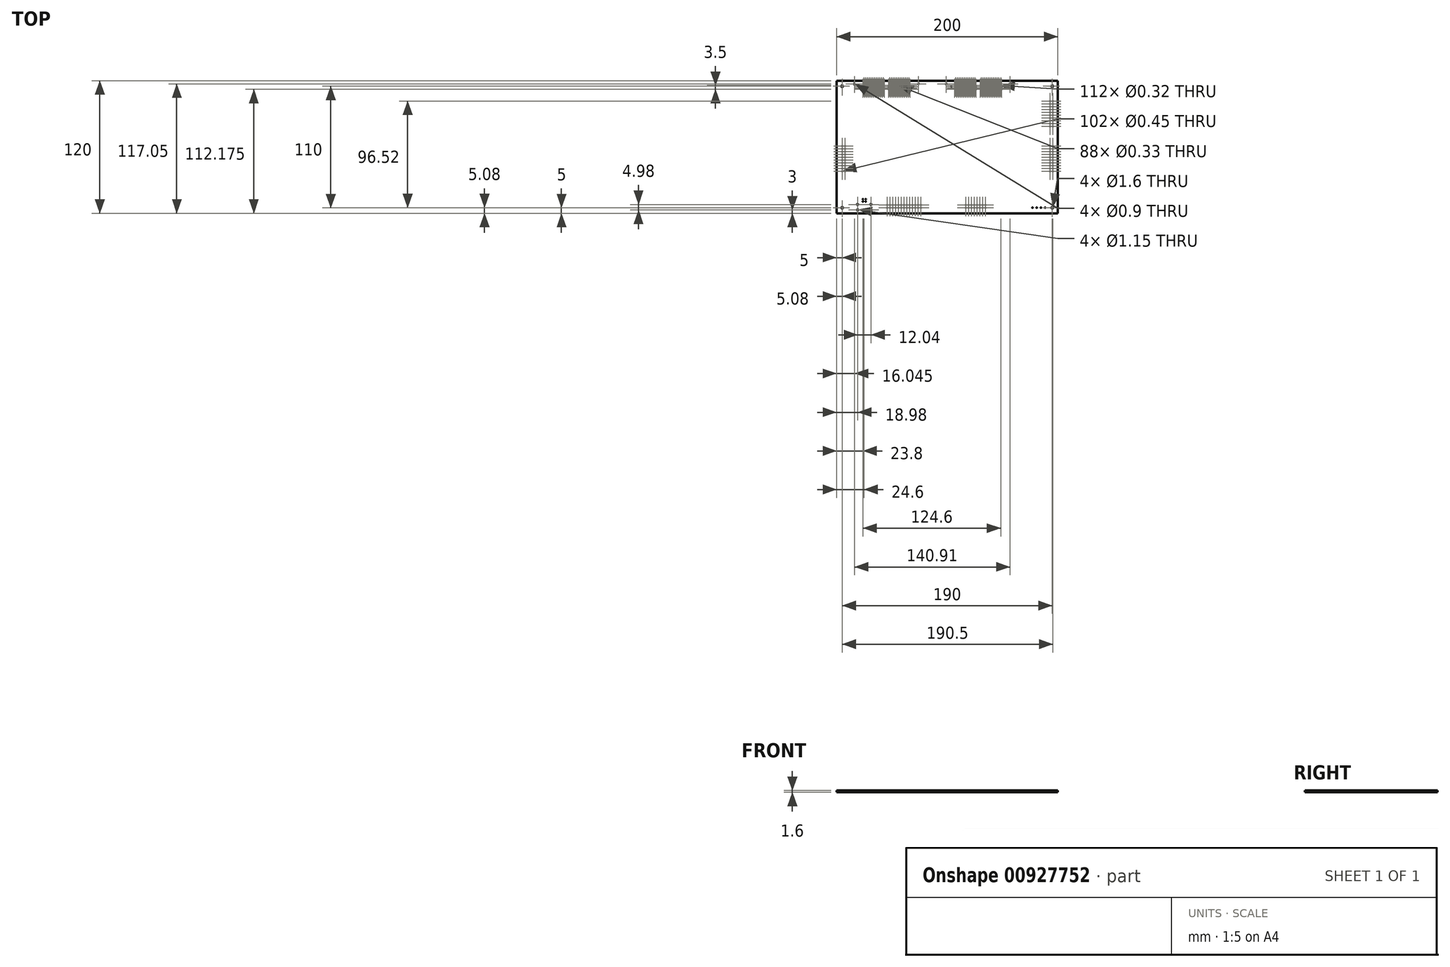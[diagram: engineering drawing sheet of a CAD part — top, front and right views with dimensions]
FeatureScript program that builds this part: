
annotation { "Feature Type Name" : "Feature", "Feature Type Description" : "" }
export const myFeature = defineFeature(function(context is Context, id is Id, definition is map)
    precondition{}
    {
        {
            var Q0;
            Q0=qCreatedBy(makeId("Top.planeOp"),FACE);
            var sketch = newSketch(context, id + "F0", { "sketchPlane" : qUnion([Q0])});
            skLineSegment(sketch, "E0", {"start": v(-100, -60) * mm, "end": v(100, -60) * mm});
            skLineSegment(sketch, "E1", {"start": v(100, -60) * mm, "end": v(100, 60) * mm});
            skLineSegment(sketch, "E2", {"start": v(100, 60) * mm, "end": v(-100, 60) * mm});
            skLineSegment(sketch, "E3", {"start": v(-100, 60) * mm, "end": v(-100, -60) * mm});
            skArc(sketch, "E4", {"start": v(-95.8, 55) * mm, "mid": v(-95, 54.2) * mm, "end": v(-94.2, 55) * mm});
            skArc(sketch, "E5", {"start": v(-94.2, 55) * mm, "mid": v(-95, 55.8) * mm, "end": v(-95.8, 55) * mm});
            skArc(sketch, "E6", {"start": v(-95.8, -55) * mm, "mid": v(-95, -55.8) * mm, "end": v(-94.2, -55) * mm});
            skArc(sketch, "E7", {"start": v(-94.2, -55) * mm, "mid": v(-95, -54.2) * mm, "end": v(-95.8, -55) * mm});
            skArc(sketch, "E8", {"start": v(94.2, -55) * mm, "mid": v(95, -55.8) * mm, "end": v(95.8, -55) * mm});
            skArc(sketch, "E9", {"start": v(95.8, -55) * mm, "mid": v(95, -54.2) * mm, "end": v(94.2, -55) * mm});
            skArc(sketch, "E10", {"start": v(94.2, 55) * mm, "mid": v(95, 54.2) * mm, "end": v(95.8, 55) * mm});
            skArc(sketch, "E11", {"start": v(95.8, 55) * mm, "mid": v(95, 55.8) * mm, "end": v(94.2, 55) * mm});
            skArc(sketch, "E12", {"start": v(-76.36, 54.53) * mm, "mid": v(-76.2, 54.36) * mm, "end": v(-76.04, 54.53) * mm});
            skArc(sketch, "E13", {"start": v(-76.04, 54.53) * mm, "mid": v(-76.2, 54.69) * mm, "end": v(-76.36, 54.53) * mm});
            skArc(sketch, "E14", {"start": v(-76.36, 52.18) * mm, "mid": v(-76.2, 52.01) * mm, "end": v(-76.04, 52.18) * mm});
            skArc(sketch, "E15", {"start": v(-76.04, 52.18) * mm, "mid": v(-76.2, 52.34) * mm, "end": v(-76.36, 52.18) * mm});
            skArc(sketch, "E16", {"start": v(-75.56, 53.33) * mm, "mid": v(-75.4, 53.16) * mm, "end": v(-75.24, 53.33) * mm});
            skArc(sketch, "E17", {"start": v(-75.24, 53.33) * mm, "mid": v(-75.4, 53.49) * mm, "end": v(-75.56, 53.33) * mm});
            skArc(sketch, "E18", {"start": v(-75.56, 55.68) * mm, "mid": v(-75.4, 55.51) * mm, "end": v(-75.24, 55.68) * mm});
            skArc(sketch, "E19", {"start": v(-75.24, 55.68) * mm, "mid": v(-75.4, 55.84) * mm, "end": v(-75.56, 55.68) * mm});
            skArc(sketch, "E20", {"start": v(-74.76, 54.53) * mm, "mid": v(-74.6, 54.36) * mm, "end": v(-74.44, 54.53) * mm});
            skArc(sketch, "E21", {"start": v(-74.44, 54.53) * mm, "mid": v(-74.6, 54.69) * mm, "end": v(-74.76, 54.53) * mm});
            skArc(sketch, "E22", {"start": v(-74.76, 52.18) * mm, "mid": v(-74.6, 52.01) * mm, "end": v(-74.44, 52.18) * mm});
            skArc(sketch, "E23", {"start": v(-74.44, 52.18) * mm, "mid": v(-74.6, 52.34) * mm, "end": v(-74.76, 52.18) * mm});
            skArc(sketch, "E24", {"start": v(-73.96, 53.33) * mm, "mid": v(-73.8, 53.16) * mm, "end": v(-73.64, 53.33) * mm});
            skArc(sketch, "E25", {"start": v(-73.64, 53.33) * mm, "mid": v(-73.8, 53.49) * mm, "end": v(-73.96, 53.33) * mm});
            skArc(sketch, "E26", {"start": v(-73.96, 55.68) * mm, "mid": v(-73.8, 55.51) * mm, "end": v(-73.64, 55.68) * mm});
            skArc(sketch, "E27", {"start": v(-73.64, 55.68) * mm, "mid": v(-73.8, 55.84) * mm, "end": v(-73.96, 55.68) * mm});
            skArc(sketch, "E28", {"start": v(-73.16, 54.53) * mm, "mid": v(-73, 54.36) * mm, "end": v(-72.84, 54.53) * mm});
            skArc(sketch, "E29", {"start": v(-72.84, 54.53) * mm, "mid": v(-73, 54.69) * mm, "end": v(-73.16, 54.53) * mm});
            skArc(sketch, "E30", {"start": v(-73.16, 52.18) * mm, "mid": v(-73, 52.01) * mm, "end": v(-72.84, 52.18) * mm});
            skArc(sketch, "E31", {"start": v(-72.84, 52.18) * mm, "mid": v(-73, 52.34) * mm, "end": v(-73.16, 52.18) * mm});
            skArc(sketch, "E32", {"start": v(-72.36, 53.33) * mm, "mid": v(-72.2, 53.16) * mm, "end": v(-72.04, 53.33) * mm});
            skArc(sketch, "E33", {"start": v(-72.04, 53.33) * mm, "mid": v(-72.2, 53.49) * mm, "end": v(-72.36, 53.33) * mm});
            skArc(sketch, "E34", {"start": v(-72.36, 55.68) * mm, "mid": v(-72.2, 55.51) * mm, "end": v(-72.04, 55.68) * mm});
            skArc(sketch, "E35", {"start": v(-72.04, 55.68) * mm, "mid": v(-72.2, 55.84) * mm, "end": v(-72.36, 55.68) * mm});
            skArc(sketch, "E36", {"start": v(-71.56, 54.53) * mm, "mid": v(-71.4, 54.36) * mm, "end": v(-71.24, 54.53) * mm});
            skArc(sketch, "E37", {"start": v(-71.24, 54.53) * mm, "mid": v(-71.4, 54.69) * mm, "end": v(-71.56, 54.53) * mm});
            skArc(sketch, "E38", {"start": v(-71.56, 52.18) * mm, "mid": v(-71.4, 52.01) * mm, "end": v(-71.24, 52.18) * mm});
            skArc(sketch, "E39", {"start": v(-71.24, 52.18) * mm, "mid": v(-71.4, 52.34) * mm, "end": v(-71.56, 52.18) * mm});
            skArc(sketch, "E40", {"start": v(-70.76, 53.33) * mm, "mid": v(-70.6, 53.16) * mm, "end": v(-70.44, 53.33) * mm});
            skArc(sketch, "E41", {"start": v(-70.44, 53.33) * mm, "mid": v(-70.6, 53.49) * mm, "end": v(-70.76, 53.33) * mm});
            skArc(sketch, "E42", {"start": v(-70.76, 55.68) * mm, "mid": v(-70.6, 55.51) * mm, "end": v(-70.44, 55.68) * mm});
            skArc(sketch, "E43", {"start": v(-70.44, 55.68) * mm, "mid": v(-70.6, 55.84) * mm, "end": v(-70.76, 55.68) * mm});
            skArc(sketch, "E44", {"start": v(-69.96, 54.53) * mm, "mid": v(-69.8, 54.36) * mm, "end": v(-69.64, 54.53) * mm});
            skArc(sketch, "E45", {"start": v(-69.64, 54.53) * mm, "mid": v(-69.8, 54.69) * mm, "end": v(-69.96, 54.53) * mm});
            skArc(sketch, "E46", {"start": v(-69.96, 52.18) * mm, "mid": v(-69.8, 52.01) * mm, "end": v(-69.64, 52.18) * mm});
            skArc(sketch, "E47", {"start": v(-69.64, 52.18) * mm, "mid": v(-69.8, 52.34) * mm, "end": v(-69.96, 52.18) * mm});
            skArc(sketch, "E48", {"start": v(-69.16, 53.33) * mm, "mid": v(-69, 53.16) * mm, "end": v(-68.84, 53.33) * mm});
            skArc(sketch, "E49", {"start": v(-68.84, 53.33) * mm, "mid": v(-69, 53.49) * mm, "end": v(-69.16, 53.33) * mm});
            skArc(sketch, "E50", {"start": v(-69.16, 55.68) * mm, "mid": v(-69, 55.51) * mm, "end": v(-68.84, 55.68) * mm});
            skArc(sketch, "E51", {"start": v(-68.84, 55.68) * mm, "mid": v(-69, 55.84) * mm, "end": v(-69.16, 55.68) * mm});
            skArc(sketch, "E52", {"start": v(-68.36, 54.53) * mm, "mid": v(-68.2, 54.36) * mm, "end": v(-68.04, 54.53) * mm});
            skArc(sketch, "E53", {"start": v(-68.04, 54.53) * mm, "mid": v(-68.2, 54.69) * mm, "end": v(-68.36, 54.53) * mm});
            skArc(sketch, "E54", {"start": v(-68.36, 52.18) * mm, "mid": v(-68.2, 52.01) * mm, "end": v(-68.04, 52.18) * mm});
            skArc(sketch, "E55", {"start": v(-68.04, 52.18) * mm, "mid": v(-68.2, 52.34) * mm, "end": v(-68.36, 52.18) * mm});
            skArc(sketch, "E56", {"start": v(-67.56, 53.33) * mm, "mid": v(-67.4, 53.16) * mm, "end": v(-67.24, 53.33) * mm});
            skArc(sketch, "E57", {"start": v(-67.24, 53.33) * mm, "mid": v(-67.4, 53.49) * mm, "end": v(-67.56, 53.33) * mm});
            skArc(sketch, "E58", {"start": v(-67.56, 55.68) * mm, "mid": v(-67.4, 55.51) * mm, "end": v(-67.24, 55.68) * mm});
            skArc(sketch, "E59", {"start": v(-67.24, 55.68) * mm, "mid": v(-67.4, 55.84) * mm, "end": v(-67.56, 55.68) * mm});
            skArc(sketch, "E60", {"start": v(-66.76, 54.53) * mm, "mid": v(-66.6, 54.36) * mm, "end": v(-66.44, 54.53) * mm});
            skArc(sketch, "E61", {"start": v(-66.44, 54.53) * mm, "mid": v(-66.6, 54.69) * mm, "end": v(-66.76, 54.53) * mm});
            skArc(sketch, "E62", {"start": v(-66.76, 52.18) * mm, "mid": v(-66.6, 52.01) * mm, "end": v(-66.44, 52.18) * mm});
            skArc(sketch, "E63", {"start": v(-66.44, 52.18) * mm, "mid": v(-66.6, 52.34) * mm, "end": v(-66.76, 52.18) * mm});
            skArc(sketch, "E64", {"start": v(-65.96, 53.33) * mm, "mid": v(-65.8, 53.16) * mm, "end": v(-65.64, 53.33) * mm});
            skArc(sketch, "E65", {"start": v(-65.64, 53.33) * mm, "mid": v(-65.8, 53.49) * mm, "end": v(-65.96, 53.33) * mm});
            skArc(sketch, "E66", {"start": v(-65.96, 55.68) * mm, "mid": v(-65.8, 55.51) * mm, "end": v(-65.64, 55.68) * mm});
            skArc(sketch, "E67", {"start": v(-65.64, 55.68) * mm, "mid": v(-65.8, 55.84) * mm, "end": v(-65.96, 55.68) * mm});
            skArc(sketch, "E68", {"start": v(-65.16, 54.53) * mm, "mid": v(-65, 54.36) * mm, "end": v(-64.84, 54.53) * mm});
            skArc(sketch, "E69", {"start": v(-64.84, 54.53) * mm, "mid": v(-65, 54.69) * mm, "end": v(-65.16, 54.53) * mm});
            skArc(sketch, "E70", {"start": v(-65.16, 52.18) * mm, "mid": v(-65, 52.01) * mm, "end": v(-64.84, 52.18) * mm});
            skArc(sketch, "E71", {"start": v(-64.84, 52.18) * mm, "mid": v(-65, 52.34) * mm, "end": v(-65.16, 52.18) * mm});
            skArc(sketch, "E72", {"start": v(-64.36, 53.33) * mm, "mid": v(-64.2, 53.16) * mm, "end": v(-64.04, 53.33) * mm});
            skArc(sketch, "E73", {"start": v(-64.04, 53.33) * mm, "mid": v(-64.2, 53.49) * mm, "end": v(-64.36, 53.33) * mm});
            skArc(sketch, "E74", {"start": v(-64.36, 55.68) * mm, "mid": v(-64.2, 55.51) * mm, "end": v(-64.04, 55.68) * mm});
            skArc(sketch, "E75", {"start": v(-64.04, 55.68) * mm, "mid": v(-64.2, 55.84) * mm, "end": v(-64.36, 55.68) * mm});
            skArc(sketch, "E76", {"start": v(-63.56, 54.53) * mm, "mid": v(-63.4, 54.36) * mm, "end": v(-63.24, 54.53) * mm});
            skArc(sketch, "E77", {"start": v(-63.24, 54.53) * mm, "mid": v(-63.4, 54.69) * mm, "end": v(-63.56, 54.53) * mm});
            skArc(sketch, "E78", {"start": v(-63.56, 52.18) * mm, "mid": v(-63.4, 52.01) * mm, "end": v(-63.24, 52.18) * mm});
            skArc(sketch, "E79", {"start": v(-63.24, 52.18) * mm, "mid": v(-63.4, 52.34) * mm, "end": v(-63.56, 52.18) * mm});
            skArc(sketch, "E80", {"start": v(-62.76, 53.33) * mm, "mid": v(-62.6, 53.16) * mm, "end": v(-62.44, 53.33) * mm});
            skArc(sketch, "E81", {"start": v(-62.44, 53.33) * mm, "mid": v(-62.6, 53.49) * mm, "end": v(-62.76, 53.33) * mm});
            skArc(sketch, "E82", {"start": v(-62.76, 55.68) * mm, "mid": v(-62.6, 55.51) * mm, "end": v(-62.44, 55.68) * mm});
            skArc(sketch, "E83", {"start": v(-62.44, 55.68) * mm, "mid": v(-62.6, 55.84) * mm, "end": v(-62.76, 55.68) * mm});
            skArc(sketch, "E84", {"start": v(-61.96, 54.53) * mm, "mid": v(-61.8, 54.36) * mm, "end": v(-61.64, 54.53) * mm});
            skArc(sketch, "E85", {"start": v(-61.64, 54.53) * mm, "mid": v(-61.8, 54.69) * mm, "end": v(-61.96, 54.53) * mm});
            skArc(sketch, "E86", {"start": v(-61.96, 52.18) * mm, "mid": v(-61.8, 52.01) * mm, "end": v(-61.64, 52.18) * mm});
            skArc(sketch, "E87", {"start": v(-61.64, 52.18) * mm, "mid": v(-61.8, 52.34) * mm, "end": v(-61.96, 52.18) * mm});
            skArc(sketch, "E88", {"start": v(-61.16, 53.33) * mm, "mid": v(-61, 53.16) * mm, "end": v(-60.84, 53.33) * mm});
            skArc(sketch, "E89", {"start": v(-60.84, 53.33) * mm, "mid": v(-61, 53.49) * mm, "end": v(-61.16, 53.33) * mm});
            skArc(sketch, "E90", {"start": v(-61.16, 55.68) * mm, "mid": v(-61, 55.51) * mm, "end": v(-60.84, 55.68) * mm});
            skArc(sketch, "E91", {"start": v(-60.84, 55.68) * mm, "mid": v(-61, 55.84) * mm, "end": v(-61.16, 55.68) * mm});
            skArc(sketch, "E92", {"start": v(-60.36, 54.53) * mm, "mid": v(-60.2, 54.36) * mm, "end": v(-60.04, 54.53) * mm});
            skArc(sketch, "E93", {"start": v(-60.04, 54.53) * mm, "mid": v(-60.2, 54.69) * mm, "end": v(-60.36, 54.53) * mm});
            skArc(sketch, "E94", {"start": v(-60.36, 52.18) * mm, "mid": v(-60.2, 52.01) * mm, "end": v(-60.04, 52.18) * mm});
            skArc(sketch, "E95", {"start": v(-60.04, 52.18) * mm, "mid": v(-60.2, 52.34) * mm, "end": v(-60.36, 52.18) * mm});
            skArc(sketch, "E96", {"start": v(-59.56, 53.33) * mm, "mid": v(-59.4, 53.16) * mm, "end": v(-59.24, 53.33) * mm});
            skArc(sketch, "E97", {"start": v(-59.24, 53.33) * mm, "mid": v(-59.4, 53.49) * mm, "end": v(-59.56, 53.33) * mm});
            skArc(sketch, "E98", {"start": v(-59.56, 55.68) * mm, "mid": v(-59.4, 55.51) * mm, "end": v(-59.24, 55.68) * mm});
            skArc(sketch, "E99", {"start": v(-59.24, 55.68) * mm, "mid": v(-59.4, 55.84) * mm, "end": v(-59.56, 55.68) * mm});
            skArc(sketch, "E100", {"start": v(-58.76, 54.53) * mm, "mid": v(-58.6, 54.36) * mm, "end": v(-58.44, 54.53) * mm});
            skArc(sketch, "E101", {"start": v(-58.44, 54.53) * mm, "mid": v(-58.6, 54.69) * mm, "end": v(-58.76, 54.53) * mm});
            skArc(sketch, "E102", {"start": v(-58.76, 52.18) * mm, "mid": v(-58.6, 52.01) * mm, "end": v(-58.44, 52.18) * mm});
            skArc(sketch, "E103", {"start": v(-58.44, 52.18) * mm, "mid": v(-58.6, 52.34) * mm, "end": v(-58.76, 52.18) * mm});
            skArc(sketch, "E104", {"start": v(-57.96, 53.33) * mm, "mid": v(-57.8, 53.16) * mm, "end": v(-57.64, 53.33) * mm});
            skArc(sketch, "E105", {"start": v(-57.64, 53.33) * mm, "mid": v(-57.8, 53.49) * mm, "end": v(-57.96, 53.33) * mm});
            skArc(sketch, "E106", {"start": v(-57.96, 55.68) * mm, "mid": v(-57.8, 55.51) * mm, "end": v(-57.64, 55.68) * mm});
            skArc(sketch, "E107", {"start": v(-57.64, 55.68) * mm, "mid": v(-57.8, 55.84) * mm, "end": v(-57.96, 55.68) * mm});
            skArc(sketch, "E108", {"start": v(-57.16, 54.53) * mm, "mid": v(-57, 54.36) * mm, "end": v(-56.84, 54.53) * mm});
            skArc(sketch, "E109", {"start": v(-56.84, 54.53) * mm, "mid": v(-57, 54.69) * mm, "end": v(-57.16, 54.53) * mm});
            skArc(sketch, "E110", {"start": v(-57.16, 52.18) * mm, "mid": v(-57, 52.01) * mm, "end": v(-56.84, 52.18) * mm});
            skArc(sketch, "E111", {"start": v(-56.84, 52.18) * mm, "mid": v(-57, 52.34) * mm, "end": v(-57.16, 52.18) * mm});
            skArc(sketch, "E112", {"start": v(-53.16, 52.18) * mm, "mid": v(-53, 52.01) * mm, "end": v(-52.84, 52.18) * mm});
            skArc(sketch, "E113", {"start": v(-52.84, 52.18) * mm, "mid": v(-53, 52.34) * mm, "end": v(-53.16, 52.18) * mm});
            skArc(sketch, "E114", {"start": v(-53.16, 54.53) * mm, "mid": v(-53, 54.36) * mm, "end": v(-52.84, 54.53) * mm});
            skArc(sketch, "E115", {"start": v(-52.84, 54.53) * mm, "mid": v(-53, 54.69) * mm, "end": v(-53.16, 54.53) * mm});
            skArc(sketch, "E116", {"start": v(-52.36, 55.68) * mm, "mid": v(-52.2, 55.51) * mm, "end": v(-52.04, 55.68) * mm});
            skArc(sketch, "E117", {"start": v(-52.04, 55.68) * mm, "mid": v(-52.2, 55.84) * mm, "end": v(-52.36, 55.68) * mm});
            skArc(sketch, "E118", {"start": v(-52.36, 53.33) * mm, "mid": v(-52.2, 53.16) * mm, "end": v(-52.04, 53.33) * mm});
            skArc(sketch, "E119", {"start": v(-52.04, 53.33) * mm, "mid": v(-52.2, 53.49) * mm, "end": v(-52.36, 53.33) * mm});
            skArc(sketch, "E120", {"start": v(-51.56, 52.18) * mm, "mid": v(-51.4, 52.01) * mm, "end": v(-51.24, 52.18) * mm});
            skArc(sketch, "E121", {"start": v(-51.24, 52.18) * mm, "mid": v(-51.4, 52.34) * mm, "end": v(-51.56, 52.18) * mm});
            skArc(sketch, "E122", {"start": v(-51.56, 54.53) * mm, "mid": v(-51.4, 54.36) * mm, "end": v(-51.24, 54.53) * mm});
            skArc(sketch, "E123", {"start": v(-51.24, 54.53) * mm, "mid": v(-51.4, 54.69) * mm, "end": v(-51.56, 54.53) * mm});
            skArc(sketch, "E124", {"start": v(-50.76, 55.68) * mm, "mid": v(-50.6, 55.51) * mm, "end": v(-50.44, 55.68) * mm});
            skArc(sketch, "E125", {"start": v(-50.44, 55.68) * mm, "mid": v(-50.6, 55.84) * mm, "end": v(-50.76, 55.68) * mm});
            skArc(sketch, "E126", {"start": v(-50.76, 53.33) * mm, "mid": v(-50.6, 53.16) * mm, "end": v(-50.44, 53.33) * mm});
            skArc(sketch, "E127", {"start": v(-50.44, 53.33) * mm, "mid": v(-50.6, 53.49) * mm, "end": v(-50.76, 53.33) * mm});
            skArc(sketch, "E128", {"start": v(-49.96, 52.18) * mm, "mid": v(-49.8, 52.01) * mm, "end": v(-49.64, 52.18) * mm});
            skArc(sketch, "E129", {"start": v(-49.64, 52.18) * mm, "mid": v(-49.8, 52.34) * mm, "end": v(-49.96, 52.18) * mm});
            skArc(sketch, "E130", {"start": v(-49.96, 54.53) * mm, "mid": v(-49.8, 54.36) * mm, "end": v(-49.64, 54.53) * mm});
            skArc(sketch, "E131", {"start": v(-49.64, 54.53) * mm, "mid": v(-49.8, 54.69) * mm, "end": v(-49.96, 54.53) * mm});
            skArc(sketch, "E132", {"start": v(-49.16, 55.68) * mm, "mid": v(-49, 55.51) * mm, "end": v(-48.84, 55.68) * mm});
            skArc(sketch, "E133", {"start": v(-48.84, 55.68) * mm, "mid": v(-49, 55.84) * mm, "end": v(-49.16, 55.68) * mm});
            skArc(sketch, "E134", {"start": v(-49.16, 53.33) * mm, "mid": v(-49, 53.16) * mm, "end": v(-48.84, 53.33) * mm});
            skArc(sketch, "E135", {"start": v(-48.84, 53.33) * mm, "mid": v(-49, 53.49) * mm, "end": v(-49.16, 53.33) * mm});
            skArc(sketch, "E136", {"start": v(-48.36, 52.18) * mm, "mid": v(-48.2, 52.01) * mm, "end": v(-48.04, 52.18) * mm});
            skArc(sketch, "E137", {"start": v(-48.04, 52.18) * mm, "mid": v(-48.2, 52.34) * mm, "end": v(-48.36, 52.18) * mm});
            skArc(sketch, "E138", {"start": v(-48.36, 54.53) * mm, "mid": v(-48.2, 54.36) * mm, "end": v(-48.04, 54.53) * mm});
            skArc(sketch, "E139", {"start": v(-48.04, 54.53) * mm, "mid": v(-48.2, 54.69) * mm, "end": v(-48.36, 54.53) * mm});
            skArc(sketch, "E140", {"start": v(-47.56, 55.68) * mm, "mid": v(-47.4, 55.51) * mm, "end": v(-47.24, 55.68) * mm});
            skArc(sketch, "E141", {"start": v(-47.24, 55.68) * mm, "mid": v(-47.4, 55.84) * mm, "end": v(-47.56, 55.68) * mm});
            skArc(sketch, "E142", {"start": v(-47.56, 53.33) * mm, "mid": v(-47.4, 53.16) * mm, "end": v(-47.24, 53.33) * mm});
            skArc(sketch, "E143", {"start": v(-47.24, 53.33) * mm, "mid": v(-47.4, 53.49) * mm, "end": v(-47.56, 53.33) * mm});
            skArc(sketch, "E144", {"start": v(-46.76, 52.18) * mm, "mid": v(-46.6, 52.01) * mm, "end": v(-46.44, 52.18) * mm});
            skArc(sketch, "E145", {"start": v(-46.44, 52.18) * mm, "mid": v(-46.6, 52.34) * mm, "end": v(-46.76, 52.18) * mm});
            skArc(sketch, "E146", {"start": v(-46.76, 54.53) * mm, "mid": v(-46.6, 54.36) * mm, "end": v(-46.44, 54.53) * mm});
            skArc(sketch, "E147", {"start": v(-46.44, 54.53) * mm, "mid": v(-46.6, 54.69) * mm, "end": v(-46.76, 54.53) * mm});
            skArc(sketch, "E148", {"start": v(-45.96, 55.68) * mm, "mid": v(-45.8, 55.51) * mm, "end": v(-45.64, 55.68) * mm});
            skArc(sketch, "E149", {"start": v(-45.64, 55.68) * mm, "mid": v(-45.8, 55.84) * mm, "end": v(-45.96, 55.68) * mm});
            skArc(sketch, "E150", {"start": v(-45.96, 53.33) * mm, "mid": v(-45.8, 53.16) * mm, "end": v(-45.64, 53.33) * mm});
            skArc(sketch, "E151", {"start": v(-45.64, 53.33) * mm, "mid": v(-45.8, 53.49) * mm, "end": v(-45.96, 53.33) * mm});
            skArc(sketch, "E152", {"start": v(-45.16, 52.18) * mm, "mid": v(-45, 52.01) * mm, "end": v(-44.84, 52.18) * mm});
            skArc(sketch, "E153", {"start": v(-44.84, 52.18) * mm, "mid": v(-45, 52.34) * mm, "end": v(-45.16, 52.18) * mm});
            skArc(sketch, "E154", {"start": v(-45.16, 54.53) * mm, "mid": v(-45, 54.36) * mm, "end": v(-44.84, 54.53) * mm});
            skArc(sketch, "E155", {"start": v(-44.84, 54.53) * mm, "mid": v(-45, 54.69) * mm, "end": v(-45.16, 54.53) * mm});
            skArc(sketch, "E156", {"start": v(-44.36, 55.68) * mm, "mid": v(-44.2, 55.51) * mm, "end": v(-44.04, 55.68) * mm});
            skArc(sketch, "E157", {"start": v(-44.04, 55.68) * mm, "mid": v(-44.2, 55.84) * mm, "end": v(-44.36, 55.68) * mm});
            skArc(sketch, "E158", {"start": v(-44.36, 53.33) * mm, "mid": v(-44.2, 53.16) * mm, "end": v(-44.04, 53.33) * mm});
            skArc(sketch, "E159", {"start": v(-44.04, 53.33) * mm, "mid": v(-44.2, 53.49) * mm, "end": v(-44.36, 53.33) * mm});
            skArc(sketch, "E160", {"start": v(-43.56, 52.18) * mm, "mid": v(-43.4, 52.01) * mm, "end": v(-43.24, 52.18) * mm});
            skArc(sketch, "E161", {"start": v(-43.24, 52.18) * mm, "mid": v(-43.4, 52.34) * mm, "end": v(-43.56, 52.18) * mm});
            skArc(sketch, "E162", {"start": v(-43.56, 54.53) * mm, "mid": v(-43.4, 54.36) * mm, "end": v(-43.24, 54.53) * mm});
            skArc(sketch, "E163", {"start": v(-43.24, 54.53) * mm, "mid": v(-43.4, 54.69) * mm, "end": v(-43.56, 54.53) * mm});
            skArc(sketch, "E164", {"start": v(-42.76, 55.68) * mm, "mid": v(-42.6, 55.51) * mm, "end": v(-42.44, 55.68) * mm});
            skArc(sketch, "E165", {"start": v(-42.44, 55.68) * mm, "mid": v(-42.6, 55.84) * mm, "end": v(-42.76, 55.68) * mm});
            skArc(sketch, "E166", {"start": v(-42.76, 53.33) * mm, "mid": v(-42.6, 53.16) * mm, "end": v(-42.44, 53.33) * mm});
            skArc(sketch, "E167", {"start": v(-42.44, 53.33) * mm, "mid": v(-42.6, 53.49) * mm, "end": v(-42.76, 53.33) * mm});
            skArc(sketch, "E168", {"start": v(-41.96, 52.18) * mm, "mid": v(-41.8, 52.01) * mm, "end": v(-41.64, 52.18) * mm});
            skArc(sketch, "E169", {"start": v(-41.64, 52.18) * mm, "mid": v(-41.8, 52.34) * mm, "end": v(-41.96, 52.18) * mm});
            skArc(sketch, "E170", {"start": v(-41.96, 54.53) * mm, "mid": v(-41.8, 54.36) * mm, "end": v(-41.64, 54.53) * mm});
            skArc(sketch, "E171", {"start": v(-41.64, 54.53) * mm, "mid": v(-41.8, 54.69) * mm, "end": v(-41.96, 54.53) * mm});
            skArc(sketch, "E172", {"start": v(-41.16, 55.68) * mm, "mid": v(-41, 55.51) * mm, "end": v(-40.84, 55.68) * mm});
            skArc(sketch, "E173", {"start": v(-40.84, 55.68) * mm, "mid": v(-41, 55.84) * mm, "end": v(-41.16, 55.68) * mm});
            skArc(sketch, "E174", {"start": v(-41.16, 53.33) * mm, "mid": v(-41, 53.16) * mm, "end": v(-40.84, 53.33) * mm});
            skArc(sketch, "E175", {"start": v(-40.84, 53.33) * mm, "mid": v(-41, 53.49) * mm, "end": v(-41.16, 53.33) * mm});
            skArc(sketch, "E176", {"start": v(-40.36, 52.18) * mm, "mid": v(-40.2, 52.01) * mm, "end": v(-40.04, 52.18) * mm});
            skArc(sketch, "E177", {"start": v(-40.04, 52.18) * mm, "mid": v(-40.2, 52.34) * mm, "end": v(-40.36, 52.18) * mm});
            skArc(sketch, "E178", {"start": v(-40.36, 54.53) * mm, "mid": v(-40.2, 54.36) * mm, "end": v(-40.04, 54.53) * mm});
            skArc(sketch, "E179", {"start": v(-40.04, 54.53) * mm, "mid": v(-40.2, 54.69) * mm, "end": v(-40.36, 54.53) * mm});
            skArc(sketch, "E180", {"start": v(-39.56, 55.68) * mm, "mid": v(-39.4, 55.51) * mm, "end": v(-39.24, 55.68) * mm});
            skArc(sketch, "E181", {"start": v(-39.24, 55.68) * mm, "mid": v(-39.4, 55.84) * mm, "end": v(-39.56, 55.68) * mm});
            skArc(sketch, "E182", {"start": v(-39.56, 53.33) * mm, "mid": v(-39.4, 53.16) * mm, "end": v(-39.24, 53.33) * mm});
            skArc(sketch, "E183", {"start": v(-39.24, 53.33) * mm, "mid": v(-39.4, 53.49) * mm, "end": v(-39.56, 53.33) * mm});
            skArc(sketch, "E184", {"start": v(-38.76, 52.18) * mm, "mid": v(-38.6, 52.01) * mm, "end": v(-38.44, 52.18) * mm});
            skArc(sketch, "E185", {"start": v(-38.44, 52.18) * mm, "mid": v(-38.6, 52.34) * mm, "end": v(-38.76, 52.18) * mm});
            skArc(sketch, "E186", {"start": v(-38.76, 54.53) * mm, "mid": v(-38.6, 54.36) * mm, "end": v(-38.44, 54.53) * mm});
            skArc(sketch, "E187", {"start": v(-38.44, 54.53) * mm, "mid": v(-38.6, 54.69) * mm, "end": v(-38.76, 54.53) * mm});
            skArc(sketch, "E188", {"start": v(-37.96, 55.68) * mm, "mid": v(-37.8, 55.51) * mm, "end": v(-37.64, 55.68) * mm});
            skArc(sketch, "E189", {"start": v(-37.64, 55.68) * mm, "mid": v(-37.8, 55.84) * mm, "end": v(-37.96, 55.68) * mm});
            skArc(sketch, "E190", {"start": v(-37.96, 53.33) * mm, "mid": v(-37.8, 53.16) * mm, "end": v(-37.64, 53.33) * mm});
            skArc(sketch, "E191", {"start": v(-37.64, 53.33) * mm, "mid": v(-37.8, 53.49) * mm, "end": v(-37.96, 53.33) * mm});
            skArc(sketch, "E192", {"start": v(-37.16, 52.18) * mm, "mid": v(-37, 52.01) * mm, "end": v(-36.84, 52.18) * mm});
            skArc(sketch, "E193", {"start": v(-36.84, 52.18) * mm, "mid": v(-37, 52.34) * mm, "end": v(-37.16, 52.18) * mm});
            skArc(sketch, "E194", {"start": v(-37.16, 54.53) * mm, "mid": v(-37, 54.36) * mm, "end": v(-36.84, 54.53) * mm});
            skArc(sketch, "E195", {"start": v(-36.84, 54.53) * mm, "mid": v(-37, 54.69) * mm, "end": v(-37.16, 54.53) * mm});
            skArc(sketch, "E196", {"start": v(-36.36, 55.68) * mm, "mid": v(-36.2, 55.51) * mm, "end": v(-36.04, 55.68) * mm});
            skArc(sketch, "E197", {"start": v(-36.04, 55.68) * mm, "mid": v(-36.2, 55.84) * mm, "end": v(-36.36, 55.68) * mm});
            skArc(sketch, "E198", {"start": v(-36.36, 53.33) * mm, "mid": v(-36.2, 53.16) * mm, "end": v(-36.04, 53.33) * mm});
            skArc(sketch, "E199", {"start": v(-36.04, 53.33) * mm, "mid": v(-36.2, 53.49) * mm, "end": v(-36.36, 53.33) * mm});
            skArc(sketch, "E200", {"start": v(-35.56, 52.18) * mm, "mid": v(-35.4, 52.01) * mm, "end": v(-35.24, 52.18) * mm});
            skArc(sketch, "E201", {"start": v(-35.24, 52.18) * mm, "mid": v(-35.4, 52.34) * mm, "end": v(-35.56, 52.18) * mm});
            skArc(sketch, "E202", {"start": v(-35.56, 54.53) * mm, "mid": v(-35.4, 54.36) * mm, "end": v(-35.24, 54.53) * mm});
            skArc(sketch, "E203", {"start": v(-35.24, 54.53) * mm, "mid": v(-35.4, 54.69) * mm, "end": v(-35.56, 54.53) * mm});
            skArc(sketch, "E204", {"start": v(-34.76, 55.68) * mm, "mid": v(-34.6, 55.51) * mm, "end": v(-34.44, 55.68) * mm});
            skArc(sketch, "E205", {"start": v(-34.44, 55.68) * mm, "mid": v(-34.6, 55.84) * mm, "end": v(-34.76, 55.68) * mm});
            skArc(sketch, "E206", {"start": v(-34.76, 53.33) * mm, "mid": v(-34.6, 53.16) * mm, "end": v(-34.44, 53.33) * mm});
            skArc(sketch, "E207", {"start": v(-34.44, 53.33) * mm, "mid": v(-34.6, 53.49) * mm, "end": v(-34.76, 53.33) * mm});
            skArc(sketch, "E208", {"start": v(-33.96, 52.18) * mm, "mid": v(-33.8, 52.01) * mm, "end": v(-33.64, 52.18) * mm});
            skArc(sketch, "E209", {"start": v(-33.64, 52.18) * mm, "mid": v(-33.8, 52.34) * mm, "end": v(-33.96, 52.18) * mm});
            skArc(sketch, "E210", {"start": v(-33.96, 54.53) * mm, "mid": v(-33.8, 54.36) * mm, "end": v(-33.64, 54.53) * mm});
            skArc(sketch, "E211", {"start": v(-33.64, 54.53) * mm, "mid": v(-33.8, 54.69) * mm, "end": v(-33.96, 54.53) * mm});
            skArc(sketch, "E212", {"start": v(6.64, 54.53) * mm, "mid": v(6.8, 54.36) * mm, "end": v(6.96, 54.53) * mm});
            skArc(sketch, "E213", {"start": v(6.96, 54.53) * mm, "mid": v(6.8, 54.69) * mm, "end": v(6.64, 54.53) * mm});
            skArc(sketch, "E214", {"start": v(6.64, 52.18) * mm, "mid": v(6.8, 52.01) * mm, "end": v(6.96, 52.18) * mm});
            skArc(sketch, "E215", {"start": v(6.96, 52.18) * mm, "mid": v(6.8, 52.34) * mm, "end": v(6.64, 52.18) * mm});
            skArc(sketch, "E216", {"start": v(7.44, 53.33) * mm, "mid": v(7.6, 53.16) * mm, "end": v(7.76, 53.33) * mm});
            skArc(sketch, "E217", {"start": v(7.76, 53.33) * mm, "mid": v(7.6, 53.49) * mm, "end": v(7.44, 53.33) * mm});
            skArc(sketch, "E218", {"start": v(7.44, 55.68) * mm, "mid": v(7.6, 55.51) * mm, "end": v(7.76, 55.68) * mm});
            skArc(sketch, "E219", {"start": v(7.76, 55.68) * mm, "mid": v(7.6, 55.84) * mm, "end": v(7.44, 55.68) * mm});
            skArc(sketch, "E220", {"start": v(8.24, 54.53) * mm, "mid": v(8.4, 54.36) * mm, "end": v(8.56, 54.53) * mm});
            skArc(sketch, "E221", {"start": v(8.56, 54.53) * mm, "mid": v(8.4, 54.69) * mm, "end": v(8.24, 54.53) * mm});
            skArc(sketch, "E222", {"start": v(8.24, 52.18) * mm, "mid": v(8.4, 52.01) * mm, "end": v(8.56, 52.18) * mm});
            skArc(sketch, "E223", {"start": v(8.56, 52.18) * mm, "mid": v(8.4, 52.34) * mm, "end": v(8.24, 52.18) * mm});
            skArc(sketch, "E224", {"start": v(9.04, 53.33) * mm, "mid": v(9.2, 53.16) * mm, "end": v(9.36, 53.33) * mm});
            skArc(sketch, "E225", {"start": v(9.36, 53.33) * mm, "mid": v(9.2, 53.49) * mm, "end": v(9.04, 53.33) * mm});
            skArc(sketch, "E226", {"start": v(9.04, 55.68) * mm, "mid": v(9.2, 55.51) * mm, "end": v(9.36, 55.68) * mm});
            skArc(sketch, "E227", {"start": v(9.36, 55.68) * mm, "mid": v(9.2, 55.84) * mm, "end": v(9.04, 55.68) * mm});
            skArc(sketch, "E228", {"start": v(9.84, 54.53) * mm, "mid": v(10, 54.36) * mm, "end": v(10.16, 54.53) * mm});
            skArc(sketch, "E229", {"start": v(10.16, 54.53) * mm, "mid": v(10, 54.69) * mm, "end": v(9.84, 54.53) * mm});
            skArc(sketch, "E230", {"start": v(9.84, 52.18) * mm, "mid": v(10, 52.01) * mm, "end": v(10.16, 52.18) * mm});
            skArc(sketch, "E231", {"start": v(10.16, 52.18) * mm, "mid": v(10, 52.34) * mm, "end": v(9.84, 52.18) * mm});
            skArc(sketch, "E232", {"start": v(10.64, 53.33) * mm, "mid": v(10.8, 53.16) * mm, "end": v(10.96, 53.33) * mm});
            skArc(sketch, "E233", {"start": v(10.96, 53.33) * mm, "mid": v(10.8, 53.49) * mm, "end": v(10.64, 53.33) * mm});
            skArc(sketch, "E234", {"start": v(10.64, 55.68) * mm, "mid": v(10.8, 55.51) * mm, "end": v(10.96, 55.68) * mm});
            skArc(sketch, "E235", {"start": v(10.96, 55.68) * mm, "mid": v(10.8, 55.84) * mm, "end": v(10.64, 55.68) * mm});
            skArc(sketch, "E236", {"start": v(11.44, 54.53) * mm, "mid": v(11.6, 54.36) * mm, "end": v(11.76, 54.53) * mm});
            skArc(sketch, "E237", {"start": v(11.76, 54.53) * mm, "mid": v(11.6, 54.69) * mm, "end": v(11.44, 54.53) * mm});
            skArc(sketch, "E238", {"start": v(11.44, 52.18) * mm, "mid": v(11.6, 52.01) * mm, "end": v(11.76, 52.18) * mm});
            skArc(sketch, "E239", {"start": v(11.76, 52.18) * mm, "mid": v(11.6, 52.34) * mm, "end": v(11.44, 52.18) * mm});
            skArc(sketch, "E240", {"start": v(12.24, 53.33) * mm, "mid": v(12.4, 53.16) * mm, "end": v(12.56, 53.33) * mm});
            skArc(sketch, "E241", {"start": v(12.56, 53.33) * mm, "mid": v(12.4, 53.49) * mm, "end": v(12.24, 53.33) * mm});
            skArc(sketch, "E242", {"start": v(12.24, 55.68) * mm, "mid": v(12.4, 55.51) * mm, "end": v(12.56, 55.68) * mm});
            skArc(sketch, "E243", {"start": v(12.56, 55.68) * mm, "mid": v(12.4, 55.84) * mm, "end": v(12.24, 55.68) * mm});
            skArc(sketch, "E244", {"start": v(13.04, 54.53) * mm, "mid": v(13.2, 54.36) * mm, "end": v(13.36, 54.53) * mm});
            skArc(sketch, "E245", {"start": v(13.36, 54.53) * mm, "mid": v(13.2, 54.69) * mm, "end": v(13.04, 54.53) * mm});
            skArc(sketch, "E246", {"start": v(13.04, 52.18) * mm, "mid": v(13.2, 52.01) * mm, "end": v(13.36, 52.18) * mm});
            skArc(sketch, "E247", {"start": v(13.36, 52.18) * mm, "mid": v(13.2, 52.34) * mm, "end": v(13.04, 52.18) * mm});
            skArc(sketch, "E248", {"start": v(13.84, 53.33) * mm, "mid": v(14, 53.16) * mm, "end": v(14.16, 53.33) * mm});
            skArc(sketch, "E249", {"start": v(14.16, 53.33) * mm, "mid": v(14, 53.49) * mm, "end": v(13.84, 53.33) * mm});
            skArc(sketch, "E250", {"start": v(13.84, 55.68) * mm, "mid": v(14, 55.51) * mm, "end": v(14.16, 55.68) * mm});
            skArc(sketch, "E251", {"start": v(14.16, 55.68) * mm, "mid": v(14, 55.84) * mm, "end": v(13.84, 55.68) * mm});
            skArc(sketch, "E252", {"start": v(14.64, 54.53) * mm, "mid": v(14.8, 54.36) * mm, "end": v(14.96, 54.53) * mm});
            skArc(sketch, "E253", {"start": v(14.96, 54.53) * mm, "mid": v(14.8, 54.69) * mm, "end": v(14.64, 54.53) * mm});
            skArc(sketch, "E254", {"start": v(14.64, 52.18) * mm, "mid": v(14.8, 52.01) * mm, "end": v(14.96, 52.18) * mm});
            skArc(sketch, "E255", {"start": v(14.96, 52.18) * mm, "mid": v(14.8, 52.34) * mm, "end": v(14.64, 52.18) * mm});
            skArc(sketch, "E256", {"start": v(15.44, 53.33) * mm, "mid": v(15.6, 53.16) * mm, "end": v(15.76, 53.33) * mm});
            skArc(sketch, "E257", {"start": v(15.76, 53.33) * mm, "mid": v(15.6, 53.49) * mm, "end": v(15.44, 53.33) * mm});
            skArc(sketch, "E258", {"start": v(15.44, 55.68) * mm, "mid": v(15.6, 55.51) * mm, "end": v(15.76, 55.68) * mm});
            skArc(sketch, "E259", {"start": v(15.76, 55.68) * mm, "mid": v(15.6, 55.84) * mm, "end": v(15.44, 55.68) * mm});
            skArc(sketch, "E260", {"start": v(16.24, 54.53) * mm, "mid": v(16.4, 54.36) * mm, "end": v(16.56, 54.53) * mm});
            skArc(sketch, "E261", {"start": v(16.56, 54.53) * mm, "mid": v(16.4, 54.69) * mm, "end": v(16.24, 54.53) * mm});
            skArc(sketch, "E262", {"start": v(16.24, 52.18) * mm, "mid": v(16.4, 52.01) * mm, "end": v(16.56, 52.18) * mm});
            skArc(sketch, "E263", {"start": v(16.56, 52.18) * mm, "mid": v(16.4, 52.34) * mm, "end": v(16.24, 52.18) * mm});
            skArc(sketch, "E264", {"start": v(17.04, 53.33) * mm, "mid": v(17.2, 53.16) * mm, "end": v(17.36, 53.33) * mm});
            skArc(sketch, "E265", {"start": v(17.36, 53.33) * mm, "mid": v(17.2, 53.49) * mm, "end": v(17.04, 53.33) * mm});
            skArc(sketch, "E266", {"start": v(17.04, 55.68) * mm, "mid": v(17.2, 55.51) * mm, "end": v(17.36, 55.68) * mm});
            skArc(sketch, "E267", {"start": v(17.36, 55.68) * mm, "mid": v(17.2, 55.84) * mm, "end": v(17.04, 55.68) * mm});
            skArc(sketch, "E268", {"start": v(17.84, 54.53) * mm, "mid": v(18, 54.36) * mm, "end": v(18.16, 54.53) * mm});
            skArc(sketch, "E269", {"start": v(18.16, 54.53) * mm, "mid": v(18, 54.69) * mm, "end": v(17.84, 54.53) * mm});
            skArc(sketch, "E270", {"start": v(17.84, 52.18) * mm, "mid": v(18, 52.01) * mm, "end": v(18.16, 52.18) * mm});
            skArc(sketch, "E271", {"start": v(18.16, 52.18) * mm, "mid": v(18, 52.34) * mm, "end": v(17.84, 52.18) * mm});
            skArc(sketch, "E272", {"start": v(18.64, 53.33) * mm, "mid": v(18.8, 53.16) * mm, "end": v(18.96, 53.33) * mm});
            skArc(sketch, "E273", {"start": v(18.96, 53.33) * mm, "mid": v(18.8, 53.49) * mm, "end": v(18.64, 53.33) * mm});
            skArc(sketch, "E274", {"start": v(18.64, 55.68) * mm, "mid": v(18.8, 55.51) * mm, "end": v(18.96, 55.68) * mm});
            skArc(sketch, "E275", {"start": v(18.96, 55.68) * mm, "mid": v(18.8, 55.84) * mm, "end": v(18.64, 55.68) * mm});
            skArc(sketch, "E276", {"start": v(19.44, 54.53) * mm, "mid": v(19.6, 54.36) * mm, "end": v(19.76, 54.53) * mm});
            skArc(sketch, "E277", {"start": v(19.76, 54.53) * mm, "mid": v(19.6, 54.69) * mm, "end": v(19.44, 54.53) * mm});
            skArc(sketch, "E278", {"start": v(19.44, 52.18) * mm, "mid": v(19.6, 52.01) * mm, "end": v(19.76, 52.18) * mm});
            skArc(sketch, "E279", {"start": v(19.76, 52.18) * mm, "mid": v(19.6, 52.34) * mm, "end": v(19.44, 52.18) * mm});
            skArc(sketch, "E280", {"start": v(20.24, 53.33) * mm, "mid": v(20.4, 53.16) * mm, "end": v(20.56, 53.33) * mm});
            skArc(sketch, "E281", {"start": v(20.56, 53.33) * mm, "mid": v(20.4, 53.49) * mm, "end": v(20.24, 53.33) * mm});
            skArc(sketch, "E282", {"start": v(20.24, 55.68) * mm, "mid": v(20.4, 55.51) * mm, "end": v(20.56, 55.68) * mm});
            skArc(sketch, "E283", {"start": v(20.56, 55.68) * mm, "mid": v(20.4, 55.84) * mm, "end": v(20.24, 55.68) * mm});
            skArc(sketch, "E284", {"start": v(21.04, 54.53) * mm, "mid": v(21.2, 54.36) * mm, "end": v(21.36, 54.53) * mm});
            skArc(sketch, "E285", {"start": v(21.36, 54.53) * mm, "mid": v(21.2, 54.69) * mm, "end": v(21.04, 54.53) * mm});
            skArc(sketch, "E286", {"start": v(21.04, 52.18) * mm, "mid": v(21.2, 52.01) * mm, "end": v(21.36, 52.18) * mm});
            skArc(sketch, "E287", {"start": v(21.36, 52.18) * mm, "mid": v(21.2, 52.34) * mm, "end": v(21.04, 52.18) * mm});
            skArc(sketch, "E288", {"start": v(21.84, 53.33) * mm, "mid": v(22, 53.16) * mm, "end": v(22.16, 53.33) * mm});
            skArc(sketch, "E289", {"start": v(22.16, 53.33) * mm, "mid": v(22, 53.49) * mm, "end": v(21.84, 53.33) * mm});
            skArc(sketch, "E290", {"start": v(21.84, 55.68) * mm, "mid": v(22, 55.51) * mm, "end": v(22.16, 55.68) * mm});
            skArc(sketch, "E291", {"start": v(22.16, 55.68) * mm, "mid": v(22, 55.84) * mm, "end": v(21.84, 55.68) * mm});
            skArc(sketch, "E292", {"start": v(22.64, 54.53) * mm, "mid": v(22.8, 54.36) * mm, "end": v(22.96, 54.53) * mm});
            skArc(sketch, "E293", {"start": v(22.96, 54.53) * mm, "mid": v(22.8, 54.69) * mm, "end": v(22.64, 54.53) * mm});
            skArc(sketch, "E294", {"start": v(22.64, 52.18) * mm, "mid": v(22.8, 52.01) * mm, "end": v(22.96, 52.18) * mm});
            skArc(sketch, "E295", {"start": v(22.96, 52.18) * mm, "mid": v(22.8, 52.34) * mm, "end": v(22.64, 52.18) * mm});
            skArc(sketch, "E296", {"start": v(23.44, 53.33) * mm, "mid": v(23.6, 53.16) * mm, "end": v(23.76, 53.33) * mm});
            skArc(sketch, "E297", {"start": v(23.76, 53.33) * mm, "mid": v(23.6, 53.49) * mm, "end": v(23.44, 53.33) * mm});
            skArc(sketch, "E298", {"start": v(23.44, 55.68) * mm, "mid": v(23.6, 55.51) * mm, "end": v(23.76, 55.68) * mm});
            skArc(sketch, "E299", {"start": v(23.76, 55.68) * mm, "mid": v(23.6, 55.84) * mm, "end": v(23.44, 55.68) * mm});
            skArc(sketch, "E300", {"start": v(24.24, 54.53) * mm, "mid": v(24.4, 54.36) * mm, "end": v(24.56, 54.53) * mm});
            skArc(sketch, "E301", {"start": v(24.56, 54.53) * mm, "mid": v(24.4, 54.69) * mm, "end": v(24.24, 54.53) * mm});
            skArc(sketch, "E302", {"start": v(24.24, 52.18) * mm, "mid": v(24.4, 52.01) * mm, "end": v(24.56, 52.18) * mm});
            skArc(sketch, "E303", {"start": v(24.56, 52.18) * mm, "mid": v(24.4, 52.34) * mm, "end": v(24.24, 52.18) * mm});
            skArc(sketch, "E304", {"start": v(25.04, 53.33) * mm, "mid": v(25.2, 53.16) * mm, "end": v(25.36, 53.33) * mm});
            skArc(sketch, "E305", {"start": v(25.36, 53.33) * mm, "mid": v(25.2, 53.49) * mm, "end": v(25.04, 53.33) * mm});
            skArc(sketch, "E306", {"start": v(25.04, 55.68) * mm, "mid": v(25.2, 55.51) * mm, "end": v(25.36, 55.68) * mm});
            skArc(sketch, "E307", {"start": v(25.36, 55.68) * mm, "mid": v(25.2, 55.84) * mm, "end": v(25.04, 55.68) * mm});
            skArc(sketch, "E308", {"start": v(25.84, 54.53) * mm, "mid": v(26, 54.36) * mm, "end": v(26.16, 54.53) * mm});
            skArc(sketch, "E309", {"start": v(26.16, 54.53) * mm, "mid": v(26, 54.69) * mm, "end": v(25.84, 54.53) * mm});
            skArc(sketch, "E310", {"start": v(25.84, 52.18) * mm, "mid": v(26, 52.01) * mm, "end": v(26.16, 52.18) * mm});
            skArc(sketch, "E311", {"start": v(26.16, 52.18) * mm, "mid": v(26, 52.34) * mm, "end": v(25.84, 52.18) * mm});
            skArc(sketch, "E312", {"start": v(29.84, 52.18) * mm, "mid": v(30, 52.01) * mm, "end": v(30.16, 52.18) * mm});
            skArc(sketch, "E313", {"start": v(30.16, 52.18) * mm, "mid": v(30, 52.34) * mm, "end": v(29.84, 52.18) * mm});
            skArc(sketch, "E314", {"start": v(29.84, 54.53) * mm, "mid": v(30, 54.36) * mm, "end": v(30.16, 54.53) * mm});
            skArc(sketch, "E315", {"start": v(30.16, 54.53) * mm, "mid": v(30, 54.69) * mm, "end": v(29.84, 54.53) * mm});
            skArc(sketch, "E316", {"start": v(30.64, 55.68) * mm, "mid": v(30.8, 55.51) * mm, "end": v(30.96, 55.68) * mm});
            skArc(sketch, "E317", {"start": v(30.96, 55.68) * mm, "mid": v(30.8, 55.84) * mm, "end": v(30.64, 55.68) * mm});
            skArc(sketch, "E318", {"start": v(30.64, 53.33) * mm, "mid": v(30.8, 53.16) * mm, "end": v(30.96, 53.33) * mm});
            skArc(sketch, "E319", {"start": v(30.96, 53.33) * mm, "mid": v(30.8, 53.49) * mm, "end": v(30.64, 53.33) * mm});
            skArc(sketch, "E320", {"start": v(31.44, 52.18) * mm, "mid": v(31.6, 52.01) * mm, "end": v(31.76, 52.18) * mm});
            skArc(sketch, "E321", {"start": v(31.76, 52.18) * mm, "mid": v(31.6, 52.34) * mm, "end": v(31.44, 52.18) * mm});
            skArc(sketch, "E322", {"start": v(31.44, 54.53) * mm, "mid": v(31.6, 54.36) * mm, "end": v(31.76, 54.53) * mm});
            skArc(sketch, "E323", {"start": v(31.76, 54.53) * mm, "mid": v(31.6, 54.69) * mm, "end": v(31.44, 54.53) * mm});
            skArc(sketch, "E324", {"start": v(32.24, 55.68) * mm, "mid": v(32.4, 55.51) * mm, "end": v(32.56, 55.68) * mm});
            skArc(sketch, "E325", {"start": v(32.56, 55.68) * mm, "mid": v(32.4, 55.84) * mm, "end": v(32.24, 55.68) * mm});
            skArc(sketch, "E326", {"start": v(32.24, 53.33) * mm, "mid": v(32.4, 53.16) * mm, "end": v(32.56, 53.33) * mm});
            skArc(sketch, "E327", {"start": v(32.56, 53.33) * mm, "mid": v(32.4, 53.49) * mm, "end": v(32.24, 53.33) * mm});
            skArc(sketch, "E328", {"start": v(33.04, 52.18) * mm, "mid": v(33.2, 52.01) * mm, "end": v(33.36, 52.18) * mm});
            skArc(sketch, "E329", {"start": v(33.36, 52.18) * mm, "mid": v(33.2, 52.34) * mm, "end": v(33.04, 52.18) * mm});
            skArc(sketch, "E330", {"start": v(33.04, 54.53) * mm, "mid": v(33.2, 54.36) * mm, "end": v(33.36, 54.53) * mm});
            skArc(sketch, "E331", {"start": v(33.36, 54.53) * mm, "mid": v(33.2, 54.69) * mm, "end": v(33.04, 54.53) * mm});
            skArc(sketch, "E332", {"start": v(33.84, 55.68) * mm, "mid": v(34, 55.51) * mm, "end": v(34.16, 55.68) * mm});
            skArc(sketch, "E333", {"start": v(34.16, 55.68) * mm, "mid": v(34, 55.84) * mm, "end": v(33.84, 55.68) * mm});
            skArc(sketch, "E334", {"start": v(33.84, 53.33) * mm, "mid": v(34, 53.16) * mm, "end": v(34.16, 53.33) * mm});
            skArc(sketch, "E335", {"start": v(34.16, 53.33) * mm, "mid": v(34, 53.49) * mm, "end": v(33.84, 53.33) * mm});
            skArc(sketch, "E336", {"start": v(34.64, 52.18) * mm, "mid": v(34.8, 52.01) * mm, "end": v(34.96, 52.18) * mm});
            skArc(sketch, "E337", {"start": v(34.96, 52.18) * mm, "mid": v(34.8, 52.34) * mm, "end": v(34.64, 52.18) * mm});
            skArc(sketch, "E338", {"start": v(34.64, 54.53) * mm, "mid": v(34.8, 54.36) * mm, "end": v(34.96, 54.53) * mm});
            skArc(sketch, "E339", {"start": v(34.96, 54.53) * mm, "mid": v(34.8, 54.69) * mm, "end": v(34.64, 54.53) * mm});
            skArc(sketch, "E340", {"start": v(35.44, 55.68) * mm, "mid": v(35.6, 55.51) * mm, "end": v(35.76, 55.68) * mm});
            skArc(sketch, "E341", {"start": v(35.76, 55.68) * mm, "mid": v(35.6, 55.84) * mm, "end": v(35.44, 55.68) * mm});
            skArc(sketch, "E342", {"start": v(35.44, 53.33) * mm, "mid": v(35.6, 53.16) * mm, "end": v(35.76, 53.33) * mm});
            skArc(sketch, "E343", {"start": v(35.76, 53.33) * mm, "mid": v(35.6, 53.49) * mm, "end": v(35.44, 53.33) * mm});
            skArc(sketch, "E344", {"start": v(36.24, 52.18) * mm, "mid": v(36.4, 52.01) * mm, "end": v(36.56, 52.18) * mm});
            skArc(sketch, "E345", {"start": v(36.56, 52.18) * mm, "mid": v(36.4, 52.34) * mm, "end": v(36.24, 52.18) * mm});
            skArc(sketch, "E346", {"start": v(36.24, 54.53) * mm, "mid": v(36.4, 54.36) * mm, "end": v(36.56, 54.53) * mm});
            skArc(sketch, "E347", {"start": v(36.56, 54.53) * mm, "mid": v(36.4, 54.69) * mm, "end": v(36.24, 54.53) * mm});
            skArc(sketch, "E348", {"start": v(37.04, 55.68) * mm, "mid": v(37.2, 55.51) * mm, "end": v(37.36, 55.68) * mm});
            skArc(sketch, "E349", {"start": v(37.36, 55.68) * mm, "mid": v(37.2, 55.84) * mm, "end": v(37.04, 55.68) * mm});
            skArc(sketch, "E350", {"start": v(37.04, 53.33) * mm, "mid": v(37.2, 53.16) * mm, "end": v(37.36, 53.33) * mm});
            skArc(sketch, "E351", {"start": v(37.36, 53.33) * mm, "mid": v(37.2, 53.49) * mm, "end": v(37.04, 53.33) * mm});
            skArc(sketch, "E352", {"start": v(37.84, 52.18) * mm, "mid": v(38, 52.01) * mm, "end": v(38.16, 52.18) * mm});
            skArc(sketch, "E353", {"start": v(38.16, 52.18) * mm, "mid": v(38, 52.34) * mm, "end": v(37.84, 52.18) * mm});
            skArc(sketch, "E354", {"start": v(37.84, 54.53) * mm, "mid": v(38, 54.36) * mm, "end": v(38.16, 54.53) * mm});
            skArc(sketch, "E355", {"start": v(38.16, 54.53) * mm, "mid": v(38, 54.69) * mm, "end": v(37.84, 54.53) * mm});
            skArc(sketch, "E356", {"start": v(38.64, 55.68) * mm, "mid": v(38.8, 55.51) * mm, "end": v(38.96, 55.68) * mm});
            skArc(sketch, "E357", {"start": v(38.96, 55.68) * mm, "mid": v(38.8, 55.84) * mm, "end": v(38.64, 55.68) * mm});
            skArc(sketch, "E358", {"start": v(38.64, 53.33) * mm, "mid": v(38.8, 53.16) * mm, "end": v(38.96, 53.33) * mm});
            skArc(sketch, "E359", {"start": v(38.96, 53.33) * mm, "mid": v(38.8, 53.49) * mm, "end": v(38.64, 53.33) * mm});
            skArc(sketch, "E360", {"start": v(39.44, 52.18) * mm, "mid": v(39.6, 52.01) * mm, "end": v(39.76, 52.18) * mm});
            skArc(sketch, "E361", {"start": v(39.76, 52.18) * mm, "mid": v(39.6, 52.34) * mm, "end": v(39.44, 52.18) * mm});
            skArc(sketch, "E362", {"start": v(39.44, 54.53) * mm, "mid": v(39.6, 54.36) * mm, "end": v(39.76, 54.53) * mm});
            skArc(sketch, "E363", {"start": v(39.76, 54.53) * mm, "mid": v(39.6, 54.69) * mm, "end": v(39.44, 54.53) * mm});
            skArc(sketch, "E364", {"start": v(40.24, 55.68) * mm, "mid": v(40.4, 55.51) * mm, "end": v(40.56, 55.68) * mm});
            skArc(sketch, "E365", {"start": v(40.56, 55.68) * mm, "mid": v(40.4, 55.84) * mm, "end": v(40.24, 55.68) * mm});
            skArc(sketch, "E366", {"start": v(40.24, 53.33) * mm, "mid": v(40.4, 53.16) * mm, "end": v(40.56, 53.33) * mm});
            skArc(sketch, "E367", {"start": v(40.56, 53.33) * mm, "mid": v(40.4, 53.49) * mm, "end": v(40.24, 53.33) * mm});
            skArc(sketch, "E368", {"start": v(41.04, 52.18) * mm, "mid": v(41.2, 52.01) * mm, "end": v(41.36, 52.18) * mm});
            skArc(sketch, "E369", {"start": v(41.36, 52.18) * mm, "mid": v(41.2, 52.34) * mm, "end": v(41.04, 52.18) * mm});
            skArc(sketch, "E370", {"start": v(41.04, 54.53) * mm, "mid": v(41.2, 54.36) * mm, "end": v(41.36, 54.53) * mm});
            skArc(sketch, "E371", {"start": v(41.36, 54.53) * mm, "mid": v(41.2, 54.69) * mm, "end": v(41.04, 54.53) * mm});
            skArc(sketch, "E372", {"start": v(41.84, 55.68) * mm, "mid": v(42, 55.51) * mm, "end": v(42.16, 55.68) * mm});
            skArc(sketch, "E373", {"start": v(42.16, 55.68) * mm, "mid": v(42, 55.84) * mm, "end": v(41.84, 55.68) * mm});
            skArc(sketch, "E374", {"start": v(41.84, 53.33) * mm, "mid": v(42, 53.16) * mm, "end": v(42.16, 53.33) * mm});
            skArc(sketch, "E375", {"start": v(42.16, 53.33) * mm, "mid": v(42, 53.49) * mm, "end": v(41.84, 53.33) * mm});
            skArc(sketch, "E376", {"start": v(42.64, 52.18) * mm, "mid": v(42.8, 52.01) * mm, "end": v(42.96, 52.18) * mm});
            skArc(sketch, "E377", {"start": v(42.96, 52.18) * mm, "mid": v(42.8, 52.34) * mm, "end": v(42.64, 52.18) * mm});
            skArc(sketch, "E378", {"start": v(42.64, 54.53) * mm, "mid": v(42.8, 54.36) * mm, "end": v(42.96, 54.53) * mm});
            skArc(sketch, "E379", {"start": v(42.96, 54.53) * mm, "mid": v(42.8, 54.69) * mm, "end": v(42.64, 54.53) * mm});
            skArc(sketch, "E380", {"start": v(43.44, 55.68) * mm, "mid": v(43.6, 55.51) * mm, "end": v(43.76, 55.68) * mm});
            skArc(sketch, "E381", {"start": v(43.76, 55.68) * mm, "mid": v(43.6, 55.84) * mm, "end": v(43.44, 55.68) * mm});
            skArc(sketch, "E382", {"start": v(43.44, 53.33) * mm, "mid": v(43.6, 53.16) * mm, "end": v(43.76, 53.33) * mm});
            skArc(sketch, "E383", {"start": v(43.76, 53.33) * mm, "mid": v(43.6, 53.49) * mm, "end": v(43.44, 53.33) * mm});
            skArc(sketch, "E384", {"start": v(44.24, 52.18) * mm, "mid": v(44.4, 52.01) * mm, "end": v(44.56, 52.18) * mm});
            skArc(sketch, "E385", {"start": v(44.56, 52.18) * mm, "mid": v(44.4, 52.34) * mm, "end": v(44.24, 52.18) * mm});
            skArc(sketch, "E386", {"start": v(44.24, 54.53) * mm, "mid": v(44.4, 54.36) * mm, "end": v(44.56, 54.53) * mm});
            skArc(sketch, "E387", {"start": v(44.56, 54.53) * mm, "mid": v(44.4, 54.69) * mm, "end": v(44.24, 54.53) * mm});
            skArc(sketch, "E388", {"start": v(45.04, 55.68) * mm, "mid": v(45.2, 55.51) * mm, "end": v(45.36, 55.68) * mm});
            skArc(sketch, "E389", {"start": v(45.36, 55.68) * mm, "mid": v(45.2, 55.84) * mm, "end": v(45.04, 55.68) * mm});
            skArc(sketch, "E390", {"start": v(45.04, 53.33) * mm, "mid": v(45.2, 53.16) * mm, "end": v(45.36, 53.33) * mm});
            skArc(sketch, "E391", {"start": v(45.36, 53.33) * mm, "mid": v(45.2, 53.49) * mm, "end": v(45.04, 53.33) * mm});
            skArc(sketch, "E392", {"start": v(45.84, 52.18) * mm, "mid": v(46, 52.01) * mm, "end": v(46.16, 52.18) * mm});
            skArc(sketch, "E393", {"start": v(46.16, 52.18) * mm, "mid": v(46, 52.34) * mm, "end": v(45.84, 52.18) * mm});
            skArc(sketch, "E394", {"start": v(45.84, 54.53) * mm, "mid": v(46, 54.36) * mm, "end": v(46.16, 54.53) * mm});
            skArc(sketch, "E395", {"start": v(46.16, 54.53) * mm, "mid": v(46, 54.69) * mm, "end": v(45.84, 54.53) * mm});
            skArc(sketch, "E396", {"start": v(46.64, 55.68) * mm, "mid": v(46.8, 55.51) * mm, "end": v(46.96, 55.68) * mm});
            skArc(sketch, "E397", {"start": v(46.96, 55.68) * mm, "mid": v(46.8, 55.84) * mm, "end": v(46.64, 55.68) * mm});
            skArc(sketch, "E398", {"start": v(46.64, 53.33) * mm, "mid": v(46.8, 53.16) * mm, "end": v(46.96, 53.33) * mm});
            skArc(sketch, "E399", {"start": v(46.96, 53.33) * mm, "mid": v(46.8, 53.49) * mm, "end": v(46.64, 53.33) * mm});
            skArc(sketch, "E400", {"start": v(47.44, 52.18) * mm, "mid": v(47.6, 52.01) * mm, "end": v(47.76, 52.18) * mm});
            skArc(sketch, "E401", {"start": v(47.76, 52.18) * mm, "mid": v(47.6, 52.34) * mm, "end": v(47.44, 52.18) * mm});
            skArc(sketch, "E402", {"start": v(47.44, 54.53) * mm, "mid": v(47.6, 54.36) * mm, "end": v(47.76, 54.53) * mm});
            skArc(sketch, "E403", {"start": v(47.76, 54.53) * mm, "mid": v(47.6, 54.69) * mm, "end": v(47.44, 54.53) * mm});
            skArc(sketch, "E404", {"start": v(48.24, 55.68) * mm, "mid": v(48.4, 55.51) * mm, "end": v(48.56, 55.68) * mm});
            skArc(sketch, "E405", {"start": v(48.56, 55.68) * mm, "mid": v(48.4, 55.84) * mm, "end": v(48.24, 55.68) * mm});
            skArc(sketch, "E406", {"start": v(48.24, 53.33) * mm, "mid": v(48.4, 53.16) * mm, "end": v(48.56, 53.33) * mm});
            skArc(sketch, "E407", {"start": v(48.56, 53.33) * mm, "mid": v(48.4, 53.49) * mm, "end": v(48.24, 53.33) * mm});
            skArc(sketch, "E408", {"start": v(49.04, 52.18) * mm, "mid": v(49.2, 52.01) * mm, "end": v(49.36, 52.18) * mm});
            skArc(sketch, "E409", {"start": v(49.36, 52.18) * mm, "mid": v(49.2, 52.34) * mm, "end": v(49.04, 52.18) * mm});
            skArc(sketch, "E410", {"start": v(49.04, 54.53) * mm, "mid": v(49.2, 54.36) * mm, "end": v(49.36, 54.53) * mm});
            skArc(sketch, "E411", {"start": v(49.36, 54.53) * mm, "mid": v(49.2, 54.69) * mm, "end": v(49.04, 54.53) * mm});
            skArc(sketch, "E412", {"start": v(-95.15, -21.9) * mm, "mid": v(-94.92, -22.13) * mm, "end": v(-94.7, -21.9) * mm});
            skArc(sketch, "E413", {"start": v(-94.7, -21.9) * mm, "mid": v(-94.92, -21.68) * mm, "end": v(-95.15, -21.9) * mm});
            skArc(sketch, "E414", {"start": v(-95.15, -19.36) * mm, "mid": v(-94.92, -19.59) * mm, "end": v(-94.7, -19.36) * mm});
            skArc(sketch, "E415", {"start": v(-94.7, -19.36) * mm, "mid": v(-94.92, -19.14) * mm, "end": v(-95.15, -19.36) * mm});
            skArc(sketch, "E416", {"start": v(-95.15, -16.82) * mm, "mid": v(-94.92, -17.05) * mm, "end": v(-94.7, -16.82) * mm});
            skArc(sketch, "E417", {"start": v(-94.7, -16.82) * mm, "mid": v(-94.92, -16.6) * mm, "end": v(-95.15, -16.82) * mm});
            skArc(sketch, "E418", {"start": v(-95.15, -14.28) * mm, "mid": v(-94.92, -14.5) * mm, "end": v(-94.7, -14.28) * mm});
            skArc(sketch, "E419", {"start": v(-94.7, -14.28) * mm, "mid": v(-94.92, -14.06) * mm, "end": v(-95.15, -14.28) * mm});
            skArc(sketch, "E420", {"start": v(-95.15, -11.74) * mm, "mid": v(-94.92, -11.97) * mm, "end": v(-94.7, -11.74) * mm});
            skArc(sketch, "E421", {"start": v(-94.7, -11.74) * mm, "mid": v(-94.92, -11.52) * mm, "end": v(-95.15, -11.74) * mm});
            skArc(sketch, "E422", {"start": v(-95.15, -9.2) * mm, "mid": v(-94.92, -9.43) * mm, "end": v(-94.7, -9.2) * mm});
            skArc(sketch, "E423", {"start": v(-94.7, -9.2) * mm, "mid": v(-94.92, -8.98) * mm, "end": v(-95.15, -9.2) * mm});
            skArc(sketch, "E424", {"start": v(-95.15, -6.66) * mm, "mid": v(-94.92, -6.89) * mm, "end": v(-94.7, -6.66) * mm});
            skArc(sketch, "E425", {"start": v(-94.7, -6.66) * mm, "mid": v(-94.92, -6.44) * mm, "end": v(-95.15, -6.66) * mm});
            skArc(sketch, "E426", {"start": v(-95.15, -4.12) * mm, "mid": v(-94.92, -4.35) * mm, "end": v(-94.7, -4.12) * mm});
            skArc(sketch, "E427", {"start": v(-94.7, -4.12) * mm, "mid": v(-94.92, -3.9) * mm, "end": v(-95.15, -4.12) * mm});
            skArc(sketch, "E428", {"start": v(-95.15, -1.58) * mm, "mid": v(-94.92, -1.8) * mm, "end": v(-94.7, -1.58) * mm});
            skArc(sketch, "E429", {"start": v(-94.7, -1.58) * mm, "mid": v(-94.92, -1.36) * mm, "end": v(-95.15, -1.58) * mm});
            skArc(sketch, "E430", {"start": v(-95.15, 0.96) * mm, "mid": v(-94.92, 0.74) * mm, "end": v(-94.7, 0.96) * mm});
            skArc(sketch, "E431", {"start": v(-94.7, 0.96) * mm, "mid": v(-94.92, 1.19) * mm, "end": v(-95.15, 0.96) * mm});
            skArc(sketch, "E432", {"start": v(-92.6, 0.96) * mm, "mid": v(-92.38, 0.74) * mm, "end": v(-92.16, 0.96) * mm});
            skArc(sketch, "E433", {"start": v(-92.16, 0.96) * mm, "mid": v(-92.38, 1.19) * mm, "end": v(-92.6, 0.96) * mm});
            skArc(sketch, "E434", {"start": v(-92.6, -1.58) * mm, "mid": v(-92.38, -1.8) * mm, "end": v(-92.16, -1.58) * mm});
            skArc(sketch, "E435", {"start": v(-92.16, -1.58) * mm, "mid": v(-92.38, -1.36) * mm, "end": v(-92.6, -1.58) * mm});
            skArc(sketch, "E436", {"start": v(-92.6, -4.12) * mm, "mid": v(-92.38, -4.35) * mm, "end": v(-92.16, -4.12) * mm});
            skArc(sketch, "E437", {"start": v(-92.16, -4.12) * mm, "mid": v(-92.38, -3.9) * mm, "end": v(-92.6, -4.12) * mm});
            skArc(sketch, "E438", {"start": v(-92.6, -6.66) * mm, "mid": v(-92.38, -6.89) * mm, "end": v(-92.16, -6.66) * mm});
            skArc(sketch, "E439", {"start": v(-92.16, -6.66) * mm, "mid": v(-92.38, -6.44) * mm, "end": v(-92.6, -6.66) * mm});
            skArc(sketch, "E440", {"start": v(-92.6, -9.2) * mm, "mid": v(-92.38, -9.43) * mm, "end": v(-92.16, -9.2) * mm});
            skArc(sketch, "E441", {"start": v(-92.16, -9.2) * mm, "mid": v(-92.38, -8.98) * mm, "end": v(-92.6, -9.2) * mm});
            skArc(sketch, "E442", {"start": v(-92.6, -11.74) * mm, "mid": v(-92.38, -11.97) * mm, "end": v(-92.16, -11.74) * mm});
            skArc(sketch, "E443", {"start": v(-92.16, -11.74) * mm, "mid": v(-92.38, -11.52) * mm, "end": v(-92.6, -11.74) * mm});
            skArc(sketch, "E444", {"start": v(-92.6, -14.28) * mm, "mid": v(-92.38, -14.5) * mm, "end": v(-92.16, -14.28) * mm});
            skArc(sketch, "E445", {"start": v(-92.16, -14.28) * mm, "mid": v(-92.38, -14.06) * mm, "end": v(-92.6, -14.28) * mm});
            skArc(sketch, "E446", {"start": v(-92.6, -16.82) * mm, "mid": v(-92.38, -17.05) * mm, "end": v(-92.16, -16.82) * mm});
            skArc(sketch, "E447", {"start": v(-92.16, -16.82) * mm, "mid": v(-92.38, -16.6) * mm, "end": v(-92.6, -16.82) * mm});
            skArc(sketch, "E448", {"start": v(-92.6, -19.36) * mm, "mid": v(-92.38, -19.59) * mm, "end": v(-92.16, -19.36) * mm});
            skArc(sketch, "E449", {"start": v(-92.16, -19.36) * mm, "mid": v(-92.38, -19.14) * mm, "end": v(-92.6, -19.36) * mm});
            skArc(sketch, "E450", {"start": v(-92.6, -21.9) * mm, "mid": v(-92.38, -22.13) * mm, "end": v(-92.16, -21.9) * mm});
            skArc(sketch, "E451", {"start": v(-92.16, -21.9) * mm, "mid": v(-92.38, -21.68) * mm, "end": v(-92.6, -21.9) * mm});
            skArc(sketch, "E452", {"start": v(-54.5, -52.38) * mm, "mid": v(-54.28, -52.6) * mm, "end": v(-54.06, -52.38) * mm});
            skArc(sketch, "E453", {"start": v(-54.06, -52.38) * mm, "mid": v(-54.28, -52.16) * mm, "end": v(-54.5, -52.38) * mm});
            skArc(sketch, "E454", {"start": v(-54.5, -54.92) * mm, "mid": v(-54.28, -55.15) * mm, "end": v(-54.06, -54.92) * mm});
            skArc(sketch, "E455", {"start": v(-54.06, -54.92) * mm, "mid": v(-54.28, -54.7) * mm, "end": v(-54.5, -54.92) * mm});
            skArc(sketch, "E456", {"start": v(-51.97, -52.38) * mm, "mid": v(-51.74, -52.6) * mm, "end": v(-51.52, -52.38) * mm});
            skArc(sketch, "E457", {"start": v(-51.52, -52.38) * mm, "mid": v(-51.74, -52.16) * mm, "end": v(-51.97, -52.38) * mm});
            skArc(sketch, "E458", {"start": v(-51.97, -54.92) * mm, "mid": v(-51.74, -55.15) * mm, "end": v(-51.52, -54.92) * mm});
            skArc(sketch, "E459", {"start": v(-51.52, -54.92) * mm, "mid": v(-51.74, -54.7) * mm, "end": v(-51.97, -54.92) * mm});
            skArc(sketch, "E460", {"start": v(-49.43, -52.38) * mm, "mid": v(-49.2, -52.6) * mm, "end": v(-48.98, -52.38) * mm});
            skArc(sketch, "E461", {"start": v(-48.98, -52.38) * mm, "mid": v(-49.2, -52.16) * mm, "end": v(-49.43, -52.38) * mm});
            skArc(sketch, "E462", {"start": v(-49.43, -54.92) * mm, "mid": v(-49.2, -55.15) * mm, "end": v(-48.98, -54.92) * mm});
            skArc(sketch, "E463", {"start": v(-48.98, -54.92) * mm, "mid": v(-49.2, -54.7) * mm, "end": v(-49.43, -54.92) * mm});
            skArc(sketch, "E464", {"start": v(-46.89, -52.38) * mm, "mid": v(-46.66, -52.6) * mm, "end": v(-46.44, -52.38) * mm});
            skArc(sketch, "E465", {"start": v(-46.44, -52.38) * mm, "mid": v(-46.66, -52.16) * mm, "end": v(-46.89, -52.38) * mm});
            skArc(sketch, "E466", {"start": v(-46.89, -54.92) * mm, "mid": v(-46.66, -55.15) * mm, "end": v(-46.44, -54.92) * mm});
            skArc(sketch, "E467", {"start": v(-46.44, -54.92) * mm, "mid": v(-46.66, -54.7) * mm, "end": v(-46.89, -54.92) * mm});
            skArc(sketch, "E468", {"start": v(-44.35, -52.38) * mm, "mid": v(-44.12, -52.6) * mm, "end": v(-43.9, -52.38) * mm});
            skArc(sketch, "E469", {"start": v(-43.9, -52.38) * mm, "mid": v(-44.12, -52.16) * mm, "end": v(-44.35, -52.38) * mm});
            skArc(sketch, "E470", {"start": v(-44.35, -54.92) * mm, "mid": v(-44.12, -55.15) * mm, "end": v(-43.9, -54.92) * mm});
            skArc(sketch, "E471", {"start": v(-43.9, -54.92) * mm, "mid": v(-44.12, -54.7) * mm, "end": v(-44.35, -54.92) * mm});
            skArc(sketch, "E472", {"start": v(-41.8, -52.38) * mm, "mid": v(-41.58, -52.6) * mm, "end": v(-41.36, -52.38) * mm});
            skArc(sketch, "E473", {"start": v(-41.36, -52.38) * mm, "mid": v(-41.58, -52.16) * mm, "end": v(-41.8, -52.38) * mm});
            skArc(sketch, "E474", {"start": v(-41.8, -54.92) * mm, "mid": v(-41.58, -55.15) * mm, "end": v(-41.36, -54.92) * mm});
            skArc(sketch, "E475", {"start": v(-41.36, -54.92) * mm, "mid": v(-41.58, -54.7) * mm, "end": v(-41.8, -54.92) * mm});
            skArc(sketch, "E476", {"start": v(-39.27, -54.92) * mm, "mid": v(-39.04, -55.15) * mm, "end": v(-38.82, -54.92) * mm});
            skArc(sketch, "E477", {"start": v(-38.82, -54.92) * mm, "mid": v(-39.04, -54.7) * mm, "end": v(-39.27, -54.92) * mm});
            skArc(sketch, "E478", {"start": v(-39.27, -52.38) * mm, "mid": v(-39.04, -52.6) * mm, "end": v(-38.82, -52.38) * mm});
            skArc(sketch, "E479", {"start": v(-38.82, -52.38) * mm, "mid": v(-39.04, -52.16) * mm, "end": v(-39.27, -52.38) * mm});
            skArc(sketch, "E480", {"start": v(-36.73, -52.38) * mm, "mid": v(-36.5, -52.6) * mm, "end": v(-36.28, -52.38) * mm});
            skArc(sketch, "E481", {"start": v(-36.28, -52.38) * mm, "mid": v(-36.5, -52.16) * mm, "end": v(-36.73, -52.38) * mm});
            skArc(sketch, "E482", {"start": v(-36.73, -54.92) * mm, "mid": v(-36.5, -55.15) * mm, "end": v(-36.28, -54.92) * mm});
            skArc(sketch, "E483", {"start": v(-36.28, -54.92) * mm, "mid": v(-36.5, -54.7) * mm, "end": v(-36.73, -54.92) * mm});
            skArc(sketch, "E484", {"start": v(-34.19, -54.92) * mm, "mid": v(-33.96, -55.15) * mm, "end": v(-33.74, -54.92) * mm});
            skArc(sketch, "E485", {"start": v(-33.74, -54.92) * mm, "mid": v(-33.96, -54.7) * mm, "end": v(-34.19, -54.92) * mm});
            skArc(sketch, "E486", {"start": v(-34.19, -52.38) * mm, "mid": v(-33.96, -52.6) * mm, "end": v(-33.74, -52.38) * mm});
            skArc(sketch, "E487", {"start": v(-33.74, -52.38) * mm, "mid": v(-33.96, -52.16) * mm, "end": v(-34.19, -52.38) * mm});
            skArc(sketch, "E488", {"start": v(-31.65, -52.38) * mm, "mid": v(-31.42, -52.6) * mm, "end": v(-31.2, -52.38) * mm});
            skArc(sketch, "E489", {"start": v(-31.2, -52.38) * mm, "mid": v(-31.42, -52.16) * mm, "end": v(-31.65, -52.38) * mm});
            skArc(sketch, "E490", {"start": v(-31.65, -54.92) * mm, "mid": v(-31.42, -55.15) * mm, "end": v(-31.2, -54.92) * mm});
            skArc(sketch, "E491", {"start": v(-31.2, -54.92) * mm, "mid": v(-31.42, -54.7) * mm, "end": v(-31.65, -54.92) * mm});
            skArc(sketch, "E492", {"start": v(-29.1, -54.92) * mm, "mid": v(-28.88, -55.15) * mm, "end": v(-28.66, -54.92) * mm});
            skArc(sketch, "E493", {"start": v(-28.66, -54.92) * mm, "mid": v(-28.88, -54.7) * mm, "end": v(-29.1, -54.92) * mm});
            skArc(sketch, "E494", {"start": v(-29.1, -52.38) * mm, "mid": v(-28.88, -52.6) * mm, "end": v(-28.66, -52.38) * mm});
            skArc(sketch, "E495", {"start": v(-28.66, -52.38) * mm, "mid": v(-28.88, -52.16) * mm, "end": v(-29.1, -52.38) * mm});
            skArc(sketch, "E496", {"start": v(-26.57, -52.38) * mm, "mid": v(-26.34, -52.6) * mm, "end": v(-26.12, -52.38) * mm});
            skArc(sketch, "E497", {"start": v(-26.12, -52.38) * mm, "mid": v(-26.34, -52.16) * mm, "end": v(-26.57, -52.38) * mm});
            skArc(sketch, "E498", {"start": v(-26.57, -54.92) * mm, "mid": v(-26.34, -55.15) * mm, "end": v(-26.12, -54.92) * mm});
            skArc(sketch, "E499", {"start": v(-26.12, -54.92) * mm, "mid": v(-26.34, -54.7) * mm, "end": v(-26.57, -54.92) * mm});
            skArc(sketch, "E500", {"start": v(-24.03, -54.92) * mm, "mid": v(-23.8, -55.15) * mm, "end": v(-23.58, -54.92) * mm});
            skArc(sketch, "E501", {"start": v(-23.58, -54.92) * mm, "mid": v(-23.8, -54.7) * mm, "end": v(-24.03, -54.92) * mm});
            skArc(sketch, "E502", {"start": v(-24.03, -52.38) * mm, "mid": v(-23.8, -52.6) * mm, "end": v(-23.58, -52.38) * mm});
            skArc(sketch, "E503", {"start": v(-23.58, -52.38) * mm, "mid": v(-23.8, -52.16) * mm, "end": v(-24.03, -52.38) * mm});
            skArc(sketch, "E504", {"start": v(16.62, -54.92) * mm, "mid": v(16.84, -55.15) * mm, "end": v(17.07, -54.92) * mm});
            skArc(sketch, "E505", {"start": v(17.07, -54.92) * mm, "mid": v(16.84, -54.7) * mm, "end": v(16.62, -54.92) * mm});
            skArc(sketch, "E506", {"start": v(16.62, -52.38) * mm, "mid": v(16.84, -52.6) * mm, "end": v(17.07, -52.38) * mm});
            skArc(sketch, "E507", {"start": v(17.07, -52.38) * mm, "mid": v(16.84, -52.16) * mm, "end": v(16.62, -52.38) * mm});
            skArc(sketch, "E508", {"start": v(19.16, -52.38) * mm, "mid": v(19.38, -52.6) * mm, "end": v(19.6, -52.38) * mm});
            skArc(sketch, "E509", {"start": v(19.6, -52.38) * mm, "mid": v(19.38, -52.16) * mm, "end": v(19.16, -52.38) * mm});
            skArc(sketch, "E510", {"start": v(19.16, -54.92) * mm, "mid": v(19.38, -55.15) * mm, "end": v(19.6, -54.92) * mm});
            skArc(sketch, "E511", {"start": v(19.6, -54.92) * mm, "mid": v(19.38, -54.7) * mm, "end": v(19.16, -54.92) * mm});
            skArc(sketch, "E512", {"start": v(21.7, -54.92) * mm, "mid": v(21.92, -55.15) * mm, "end": v(22.15, -54.92) * mm});
            skArc(sketch, "E513", {"start": v(22.15, -54.92) * mm, "mid": v(21.92, -54.7) * mm, "end": v(21.7, -54.92) * mm});
            skArc(sketch, "E514", {"start": v(21.7, -52.38) * mm, "mid": v(21.92, -52.6) * mm, "end": v(22.15, -52.38) * mm});
            skArc(sketch, "E515", {"start": v(22.15, -52.38) * mm, "mid": v(21.92, -52.16) * mm, "end": v(21.7, -52.38) * mm});
            skArc(sketch, "E516", {"start": v(24.24, -52.38) * mm, "mid": v(24.46, -52.6) * mm, "end": v(24.69, -52.38) * mm});
            skArc(sketch, "E517", {"start": v(24.69, -52.38) * mm, "mid": v(24.46, -52.16) * mm, "end": v(24.24, -52.38) * mm});
            skArc(sketch, "E518", {"start": v(24.24, -54.92) * mm, "mid": v(24.46, -55.15) * mm, "end": v(24.69, -54.92) * mm});
            skArc(sketch, "E519", {"start": v(24.69, -54.92) * mm, "mid": v(24.46, -54.7) * mm, "end": v(24.24, -54.92) * mm});
            skArc(sketch, "E520", {"start": v(26.78, -54.92) * mm, "mid": v(27, -55.15) * mm, "end": v(27.23, -54.92) * mm});
            skArc(sketch, "E521", {"start": v(27.23, -54.92) * mm, "mid": v(27, -54.7) * mm, "end": v(26.78, -54.92) * mm});
            skArc(sketch, "E522", {"start": v(26.78, -52.38) * mm, "mid": v(27, -52.6) * mm, "end": v(27.23, -52.38) * mm});
            skArc(sketch, "E523", {"start": v(27.23, -52.38) * mm, "mid": v(27, -52.16) * mm, "end": v(26.78, -52.38) * mm});
            skArc(sketch, "E524", {"start": v(29.32, -54.92) * mm, "mid": v(29.54, -55.15) * mm, "end": v(29.77, -54.92) * mm});
            skArc(sketch, "E525", {"start": v(29.77, -54.92) * mm, "mid": v(29.54, -54.7) * mm, "end": v(29.32, -54.92) * mm});
            skArc(sketch, "E526", {"start": v(29.32, -52.38) * mm, "mid": v(29.54, -52.6) * mm, "end": v(29.77, -52.38) * mm});
            skArc(sketch, "E527", {"start": v(29.77, -52.38) * mm, "mid": v(29.54, -52.16) * mm, "end": v(29.32, -52.38) * mm});
            skArc(sketch, "E528", {"start": v(31.86, -54.92) * mm, "mid": v(32.08, -55.15) * mm, "end": v(32.3, -54.92) * mm});
            skArc(sketch, "E529", {"start": v(32.3, -54.92) * mm, "mid": v(32.08, -54.7) * mm, "end": v(31.86, -54.92) * mm});
            skArc(sketch, "E530", {"start": v(31.86, -52.38) * mm, "mid": v(32.08, -52.6) * mm, "end": v(32.3, -52.38) * mm});
            skArc(sketch, "E531", {"start": v(32.3, -52.38) * mm, "mid": v(32.08, -52.16) * mm, "end": v(31.86, -52.38) * mm});
            skArc(sketch, "E532", {"start": v(34.4, -54.92) * mm, "mid": v(34.62, -55.15) * mm, "end": v(34.85, -54.92) * mm});
            skArc(sketch, "E533", {"start": v(34.85, -54.92) * mm, "mid": v(34.62, -54.7) * mm, "end": v(34.4, -54.92) * mm});
            skArc(sketch, "E534", {"start": v(34.4, -52.38) * mm, "mid": v(34.62, -52.6) * mm, "end": v(34.85, -52.38) * mm});
            skArc(sketch, "E535", {"start": v(34.85, -52.38) * mm, "mid": v(34.62, -52.16) * mm, "end": v(34.4, -52.38) * mm});
            skArc(sketch, "E536", {"start": v(92.82, -21.9) * mm, "mid": v(93.04, -22.13) * mm, "end": v(93.27, -21.9) * mm});
            skArc(sketch, "E537", {"start": v(93.27, -21.9) * mm, "mid": v(93.04, -21.68) * mm, "end": v(92.82, -21.9) * mm});
            skArc(sketch, "E538", {"start": v(92.82, -19.36) * mm, "mid": v(93.04, -19.59) * mm, "end": v(93.27, -19.36) * mm});
            skArc(sketch, "E539", {"start": v(93.27, -19.36) * mm, "mid": v(93.04, -19.14) * mm, "end": v(92.82, -19.36) * mm});
            skArc(sketch, "E540", {"start": v(92.82, -16.82) * mm, "mid": v(93.04, -17.05) * mm, "end": v(93.27, -16.82) * mm});
            skArc(sketch, "E541", {"start": v(93.27, -16.82) * mm, "mid": v(93.04, -16.6) * mm, "end": v(92.82, -16.82) * mm});
            skArc(sketch, "E542", {"start": v(92.82, -14.28) * mm, "mid": v(93.04, -14.5) * mm, "end": v(93.27, -14.28) * mm});
            skArc(sketch, "E543", {"start": v(93.27, -14.28) * mm, "mid": v(93.04, -14.06) * mm, "end": v(92.82, -14.28) * mm});
            skArc(sketch, "E544", {"start": v(92.82, -11.74) * mm, "mid": v(93.04, -11.97) * mm, "end": v(93.27, -11.74) * mm});
            skArc(sketch, "E545", {"start": v(93.27, -11.74) * mm, "mid": v(93.04, -11.52) * mm, "end": v(92.82, -11.74) * mm});
            skArc(sketch, "E546", {"start": v(92.82, -9.2) * mm, "mid": v(93.04, -9.43) * mm, "end": v(93.27, -9.2) * mm});
            skArc(sketch, "E547", {"start": v(93.27, -9.2) * mm, "mid": v(93.04, -8.98) * mm, "end": v(92.82, -9.2) * mm});
            skArc(sketch, "E548", {"start": v(92.82, -6.66) * mm, "mid": v(93.04, -6.89) * mm, "end": v(93.27, -6.66) * mm});
            skArc(sketch, "E549", {"start": v(93.27, -6.66) * mm, "mid": v(93.04, -6.44) * mm, "end": v(92.82, -6.66) * mm});
            skArc(sketch, "E550", {"start": v(92.82, -4.12) * mm, "mid": v(93.04, -4.35) * mm, "end": v(93.27, -4.12) * mm});
            skArc(sketch, "E551", {"start": v(93.27, -4.12) * mm, "mid": v(93.04, -3.9) * mm, "end": v(92.82, -4.12) * mm});
            skArc(sketch, "E552", {"start": v(92.82, -1.58) * mm, "mid": v(93.04, -1.8) * mm, "end": v(93.27, -1.58) * mm});
            skArc(sketch, "E553", {"start": v(93.27, -1.58) * mm, "mid": v(93.04, -1.36) * mm, "end": v(92.82, -1.58) * mm});
            skArc(sketch, "E554", {"start": v(92.82, 0.96) * mm, "mid": v(93.04, 0.74) * mm, "end": v(93.27, 0.96) * mm});
            skArc(sketch, "E555", {"start": v(93.27, 0.96) * mm, "mid": v(93.04, 1.19) * mm, "end": v(92.82, 0.96) * mm});
            skArc(sketch, "E556", {"start": v(92.82, 18.74) * mm, "mid": v(93.04, 18.52) * mm, "end": v(93.27, 18.74) * mm});
            skArc(sketch, "E557", {"start": v(93.27, 18.74) * mm, "mid": v(93.04, 18.97) * mm, "end": v(92.82, 18.74) * mm});
            skArc(sketch, "E558", {"start": v(92.82, 21.28) * mm, "mid": v(93.04, 21.06) * mm, "end": v(93.27, 21.28) * mm});
            skArc(sketch, "E559", {"start": v(93.27, 21.28) * mm, "mid": v(93.04, 21.5) * mm, "end": v(92.82, 21.28) * mm});
            skArc(sketch, "E560", {"start": v(92.82, 23.82) * mm, "mid": v(93.04, 23.6) * mm, "end": v(93.27, 23.82) * mm});
            skArc(sketch, "E561", {"start": v(93.27, 23.82) * mm, "mid": v(93.04, 24.05) * mm, "end": v(92.82, 23.82) * mm});
            skArc(sketch, "E562", {"start": v(92.82, 26.36) * mm, "mid": v(93.04, 26.14) * mm, "end": v(93.27, 26.36) * mm});
            skArc(sketch, "E563", {"start": v(93.27, 26.36) * mm, "mid": v(93.04, 26.59) * mm, "end": v(92.82, 26.36) * mm});
            skArc(sketch, "E564", {"start": v(92.82, 28.9) * mm, "mid": v(93.04, 28.68) * mm, "end": v(93.27, 28.9) * mm});
            skArc(sketch, "E565", {"start": v(93.27, 28.9) * mm, "mid": v(93.04, 29.13) * mm, "end": v(92.82, 28.9) * mm});
            skArc(sketch, "E566", {"start": v(92.82, 31.44) * mm, "mid": v(93.04, 31.22) * mm, "end": v(93.27, 31.44) * mm});
            skArc(sketch, "E567", {"start": v(93.27, 31.44) * mm, "mid": v(93.04, 31.67) * mm, "end": v(92.82, 31.44) * mm});
            skArc(sketch, "E568", {"start": v(92.82, 33.98) * mm, "mid": v(93.04, 33.76) * mm, "end": v(93.27, 33.98) * mm});
            skArc(sketch, "E569", {"start": v(93.27, 33.98) * mm, "mid": v(93.04, 34.2) * mm, "end": v(92.82, 33.98) * mm});
            skArc(sketch, "E570", {"start": v(92.82, 36.52) * mm, "mid": v(93.04, 36.3) * mm, "end": v(93.27, 36.52) * mm});
            skArc(sketch, "E571", {"start": v(93.27, 36.52) * mm, "mid": v(93.04, 36.75) * mm, "end": v(92.82, 36.52) * mm});
            skArc(sketch, "E572", {"start": v(92.82, 39.06) * mm, "mid": v(93.04, 38.84) * mm, "end": v(93.27, 39.06) * mm});
            skArc(sketch, "E573", {"start": v(93.27, 39.06) * mm, "mid": v(93.04, 39.29) * mm, "end": v(92.82, 39.06) * mm});
            skArc(sketch, "E574", {"start": v(92.82, 41.6) * mm, "mid": v(93.04, 41.38) * mm, "end": v(93.27, 41.6) * mm});
            skArc(sketch, "E575", {"start": v(93.27, 41.6) * mm, "mid": v(93.04, 41.83) * mm, "end": v(92.82, 41.6) * mm});
            skArc(sketch, "E576", {"start": v(95.36, 41.6) * mm, "mid": v(95.58, 41.38) * mm, "end": v(95.8, 41.6) * mm});
            skArc(sketch, "E577", {"start": v(95.8, 41.6) * mm, "mid": v(95.58, 41.83) * mm, "end": v(95.36, 41.6) * mm});
            skArc(sketch, "E578", {"start": v(95.36, 39.06) * mm, "mid": v(95.58, 38.84) * mm, "end": v(95.8, 39.06) * mm});
            skArc(sketch, "E579", {"start": v(95.8, 39.06) * mm, "mid": v(95.58, 39.29) * mm, "end": v(95.36, 39.06) * mm});
            skArc(sketch, "E580", {"start": v(95.36, 36.52) * mm, "mid": v(95.58, 36.3) * mm, "end": v(95.8, 36.52) * mm});
            skArc(sketch, "E581", {"start": v(95.8, 36.52) * mm, "mid": v(95.58, 36.75) * mm, "end": v(95.36, 36.52) * mm});
            skArc(sketch, "E582", {"start": v(95.36, 33.98) * mm, "mid": v(95.58, 33.76) * mm, "end": v(95.8, 33.98) * mm});
            skArc(sketch, "E583", {"start": v(95.8, 33.98) * mm, "mid": v(95.58, 34.2) * mm, "end": v(95.36, 33.98) * mm});
            skArc(sketch, "E584", {"start": v(95.36, 31.44) * mm, "mid": v(95.58, 31.22) * mm, "end": v(95.8, 31.44) * mm});
            skArc(sketch, "E585", {"start": v(95.8, 31.44) * mm, "mid": v(95.58, 31.67) * mm, "end": v(95.36, 31.44) * mm});
            skArc(sketch, "E586", {"start": v(95.36, 28.9) * mm, "mid": v(95.58, 28.68) * mm, "end": v(95.8, 28.9) * mm});
            skArc(sketch, "E587", {"start": v(95.8, 28.9) * mm, "mid": v(95.58, 29.13) * mm, "end": v(95.36, 28.9) * mm});
            skArc(sketch, "E588", {"start": v(95.36, 26.36) * mm, "mid": v(95.58, 26.14) * mm, "end": v(95.8, 26.36) * mm});
            skArc(sketch, "E589", {"start": v(95.8, 26.36) * mm, "mid": v(95.58, 26.59) * mm, "end": v(95.36, 26.36) * mm});
            skArc(sketch, "E590", {"start": v(95.36, 23.82) * mm, "mid": v(95.58, 23.6) * mm, "end": v(95.8, 23.82) * mm});
            skArc(sketch, "E591", {"start": v(95.8, 23.82) * mm, "mid": v(95.58, 24.05) * mm, "end": v(95.36, 23.82) * mm});
            skArc(sketch, "E592", {"start": v(95.36, 21.28) * mm, "mid": v(95.58, 21.06) * mm, "end": v(95.8, 21.28) * mm});
            skArc(sketch, "E593", {"start": v(95.8, 21.28) * mm, "mid": v(95.58, 21.5) * mm, "end": v(95.36, 21.28) * mm});
            skArc(sketch, "E594", {"start": v(95.36, 18.74) * mm, "mid": v(95.58, 18.52) * mm, "end": v(95.8, 18.74) * mm});
            skArc(sketch, "E595", {"start": v(95.8, 18.74) * mm, "mid": v(95.58, 18.97) * mm, "end": v(95.36, 18.74) * mm});
            skArc(sketch, "E596", {"start": v(95.36, 0.96) * mm, "mid": v(95.58, 0.74) * mm, "end": v(95.8, 0.96) * mm});
            skArc(sketch, "E597", {"start": v(95.8, 0.96) * mm, "mid": v(95.58, 1.19) * mm, "end": v(95.36, 0.96) * mm});
            skArc(sketch, "E598", {"start": v(95.36, -1.58) * mm, "mid": v(95.58, -1.8) * mm, "end": v(95.8, -1.58) * mm});
            skArc(sketch, "E599", {"start": v(95.8, -1.58) * mm, "mid": v(95.58, -1.36) * mm, "end": v(95.36, -1.58) * mm});
            skArc(sketch, "E600", {"start": v(95.36, -4.12) * mm, "mid": v(95.58, -4.35) * mm, "end": v(95.8, -4.12) * mm});
            skArc(sketch, "E601", {"start": v(95.8, -4.12) * mm, "mid": v(95.58, -3.9) * mm, "end": v(95.36, -4.12) * mm});
            skArc(sketch, "E602", {"start": v(95.36, -6.66) * mm, "mid": v(95.58, -6.89) * mm, "end": v(95.8, -6.66) * mm});
            skArc(sketch, "E603", {"start": v(95.8, -6.66) * mm, "mid": v(95.58, -6.44) * mm, "end": v(95.36, -6.66) * mm});
            skArc(sketch, "E604", {"start": v(95.36, -9.2) * mm, "mid": v(95.58, -9.43) * mm, "end": v(95.8, -9.2) * mm});
            skArc(sketch, "E605", {"start": v(95.8, -9.2) * mm, "mid": v(95.58, -8.98) * mm, "end": v(95.36, -9.2) * mm});
            skArc(sketch, "E606", {"start": v(95.36, -11.74) * mm, "mid": v(95.58, -11.97) * mm, "end": v(95.8, -11.74) * mm});
            skArc(sketch, "E607", {"start": v(95.8, -11.74) * mm, "mid": v(95.58, -11.52) * mm, "end": v(95.36, -11.74) * mm});
            skArc(sketch, "E608", {"start": v(95.36, -14.28) * mm, "mid": v(95.58, -14.5) * mm, "end": v(95.8, -14.28) * mm});
            skArc(sketch, "E609", {"start": v(95.8, -14.28) * mm, "mid": v(95.58, -14.06) * mm, "end": v(95.36, -14.28) * mm});
            skArc(sketch, "E610", {"start": v(95.36, -16.82) * mm, "mid": v(95.58, -17.05) * mm, "end": v(95.8, -16.82) * mm});
            skArc(sketch, "E611", {"start": v(95.8, -16.82) * mm, "mid": v(95.58, -16.6) * mm, "end": v(95.36, -16.82) * mm});
            skArc(sketch, "E612", {"start": v(95.36, -19.36) * mm, "mid": v(95.58, -19.59) * mm, "end": v(95.8, -19.36) * mm});
            skArc(sketch, "E613", {"start": v(95.8, -19.36) * mm, "mid": v(95.58, -19.14) * mm, "end": v(95.36, -19.36) * mm});
            skArc(sketch, "E614", {"start": v(95.36, -21.9) * mm, "mid": v(95.58, -22.13) * mm, "end": v(95.8, -21.9) * mm});
            skArc(sketch, "E615", {"start": v(95.8, -21.9) * mm, "mid": v(95.58, -21.68) * mm, "end": v(95.36, -21.9) * mm});
            skArc(sketch, "E616", {"start": v(-76.5, -49.31) * mm, "mid": v(-76.25, -49.56) * mm, "end": v(-76, -49.31) * mm});
            skArc(sketch, "E617", {"start": v(-76, -49.31) * mm, "mid": v(-76.25, -49.06) * mm, "end": v(-76.5, -49.31) * mm});
            skArc(sketch, "E618", {"start": v(-76.5, -47.31) * mm, "mid": v(-76.25, -47.56) * mm, "end": v(-76, -47.31) * mm});
            skArc(sketch, "E619", {"start": v(-76, -47.31) * mm, "mid": v(-76.25, -47.06) * mm, "end": v(-76.5, -47.31) * mm});
            skArc(sketch, "E620", {"start": v(-74, -47.31) * mm, "mid": v(-73.75, -47.56) * mm, "end": v(-73.5, -47.31) * mm});
            skArc(sketch, "E621", {"start": v(-73.5, -47.31) * mm, "mid": v(-73.75, -47.06) * mm, "end": v(-74, -47.31) * mm});
            skArc(sketch, "E622", {"start": v(-74, -49.31) * mm, "mid": v(-73.75, -49.56) * mm, "end": v(-73.5, -49.31) * mm});
            skArc(sketch, "E623", {"start": v(-73.5, -49.31) * mm, "mid": v(-73.75, -49.06) * mm, "end": v(-74, -49.31) * mm});
            skArc(sketch, "E624", {"start": v(76.9, -54.92) * mm, "mid": v(77.17, -55.2) * mm, "end": v(77.44, -54.92) * mm});
            skArc(sketch, "E625", {"start": v(77.44, -54.92) * mm, "mid": v(77.17, -54.65) * mm, "end": v(76.9, -54.92) * mm});
            skArc(sketch, "E626", {"start": v(80.7, -54.92) * mm, "mid": v(80.98, -55.2) * mm, "end": v(81.25, -54.92) * mm});
            skArc(sketch, "E627", {"start": v(81.25, -54.92) * mm, "mid": v(80.98, -54.65) * mm, "end": v(80.7, -54.92) * mm});
            skArc(sketch, "E628", {"start": v(84.51, -54.92) * mm, "mid": v(84.79, -55.2) * mm, "end": v(85.06, -54.92) * mm});
            skArc(sketch, "E629", {"start": v(85.06, -54.92) * mm, "mid": v(84.79, -54.65) * mm, "end": v(84.51, -54.92) * mm});
            skArc(sketch, "E630", {"start": v(88.32, -54.92) * mm, "mid": v(88.6, -55.2) * mm, "end": v(88.87, -54.92) * mm});
            skArc(sketch, "E631", {"start": v(88.87, -54.92) * mm, "mid": v(88.6, -54.65) * mm, "end": v(88.32, -54.92) * mm});
            skArc(sketch, "E632", {"start": v(-79.48, 54.43) * mm, "mid": v(-79.18, 54.13) * mm, "end": v(-78.88, 54.43) * mm});
            skArc(sketch, "E633", {"start": v(-78.88, 54.43) * mm, "mid": v(-79.18, 54.73) * mm, "end": v(-79.48, 54.43) * mm});
            skArc(sketch, "E634", {"start": v(-31.12, 54.43) * mm, "mid": v(-30.82, 54.13) * mm, "end": v(-30.52, 54.43) * mm});
            skArc(sketch, "E635", {"start": v(-30.52, 54.43) * mm, "mid": v(-30.82, 54.73) * mm, "end": v(-31.12, 54.43) * mm});
            skArc(sketch, "E636", {"start": v(3.52, 54.43) * mm, "mid": v(3.82, 54.13) * mm, "end": v(4.12, 54.43) * mm});
            skArc(sketch, "E637", {"start": v(4.12, 54.43) * mm, "mid": v(3.82, 54.73) * mm, "end": v(3.52, 54.43) * mm});
            skArc(sketch, "E638", {"start": v(51.88, 54.43) * mm, "mid": v(52.18, 54.13) * mm, "end": v(52.48, 54.43) * mm});
            skArc(sketch, "E639", {"start": v(52.48, 54.43) * mm, "mid": v(52.18, 54.73) * mm, "end": v(51.88, 54.43) * mm});
            skArc(sketch, "E640", {"start": v(-84.4, 57.05) * mm, "mid": v(-83.96, 56.6) * mm, "end": v(-83.5, 57.05) * mm});
            skArc(sketch, "E641", {"start": v(-83.5, 57.05) * mm, "mid": v(-83.96, 57.5) * mm, "end": v(-84.4, 57.05) * mm});
            skArc(sketch, "E642", {"start": v(-26.5, 57.05) * mm, "mid": v(-26.05, 56.6) * mm, "end": v(-25.6, 57.05) * mm});
            skArc(sketch, "E643", {"start": v(-25.6, 57.05) * mm, "mid": v(-26.05, 57.5) * mm, "end": v(-26.5, 57.05) * mm});
            skArc(sketch, "E644", {"start": v(-1.4, 57.05) * mm, "mid": v(-0.96, 56.6) * mm, "end": v(-0.5, 57.05) * mm});
            skArc(sketch, "E645", {"start": v(-0.5, 57.05) * mm, "mid": v(-0.96, 57.5) * mm, "end": v(-1.4, 57.05) * mm});
            skArc(sketch, "E646", {"start": v(56.5, 57.05) * mm, "mid": v(56.96, 56.6) * mm, "end": v(57.4, 57.05) * mm});
            skArc(sketch, "E647", {"start": v(57.4, 57.05) * mm, "mid": v(56.96, 57.5) * mm, "end": v(56.5, 57.05) * mm});
            skArc(sketch, "E648", {"start": v(-81.6, -52.02) * mm, "mid": v(-81.02, -52.6) * mm, "end": v(-80.45, -52.02) * mm});
            skArc(sketch, "E649", {"start": v(-80.45, -52.02) * mm, "mid": v(-81.02, -51.45) * mm, "end": v(-81.6, -52.02) * mm});
            skArc(sketch, "E650", {"start": v(-81.6, -57) * mm, "mid": v(-81.02, -57.58) * mm, "end": v(-80.45, -57) * mm});
            skArc(sketch, "E651", {"start": v(-80.45, -57) * mm, "mid": v(-81.02, -56.43) * mm, "end": v(-81.6, -57) * mm});
            skArc(sketch, "E652", {"start": v(-69.56, -57) * mm, "mid": v(-68.98, -57.58) * mm, "end": v(-68.4, -57) * mm});
            skArc(sketch, "E653", {"start": v(-68.4, -57) * mm, "mid": v(-68.98, -56.43) * mm, "end": v(-69.56, -57) * mm});
            skArc(sketch, "E654", {"start": v(-69.56, -52.02) * mm, "mid": v(-68.98, -52.6) * mm, "end": v(-68.4, -52.02) * mm});
            skArc(sketch, "E655", {"start": v(-68.4, -52.02) * mm, "mid": v(-68.98, -51.45) * mm, "end": v(-69.56, -52.02) * mm});
            skSolve(sketch);
        }
        {
            var Q0;
            Q0=makeQuery(id+"F0.imprint","IMPRINT",FACE,{"disambiguationData":[TD([[makeQuery(id+"F0.imprint","IMPRINT",EDGE,{"derivedFrom":sQuery(id+"F0.wireOp",EDGE,"E0")}),1.0]])]});
            extrude(context, id + "F1", {"entities" : qUnion([Q0]), "oppositeDirection" : true, "depth" : 1.6 * mm, "offsetDistance" : 25 * mm});
        }
    });
